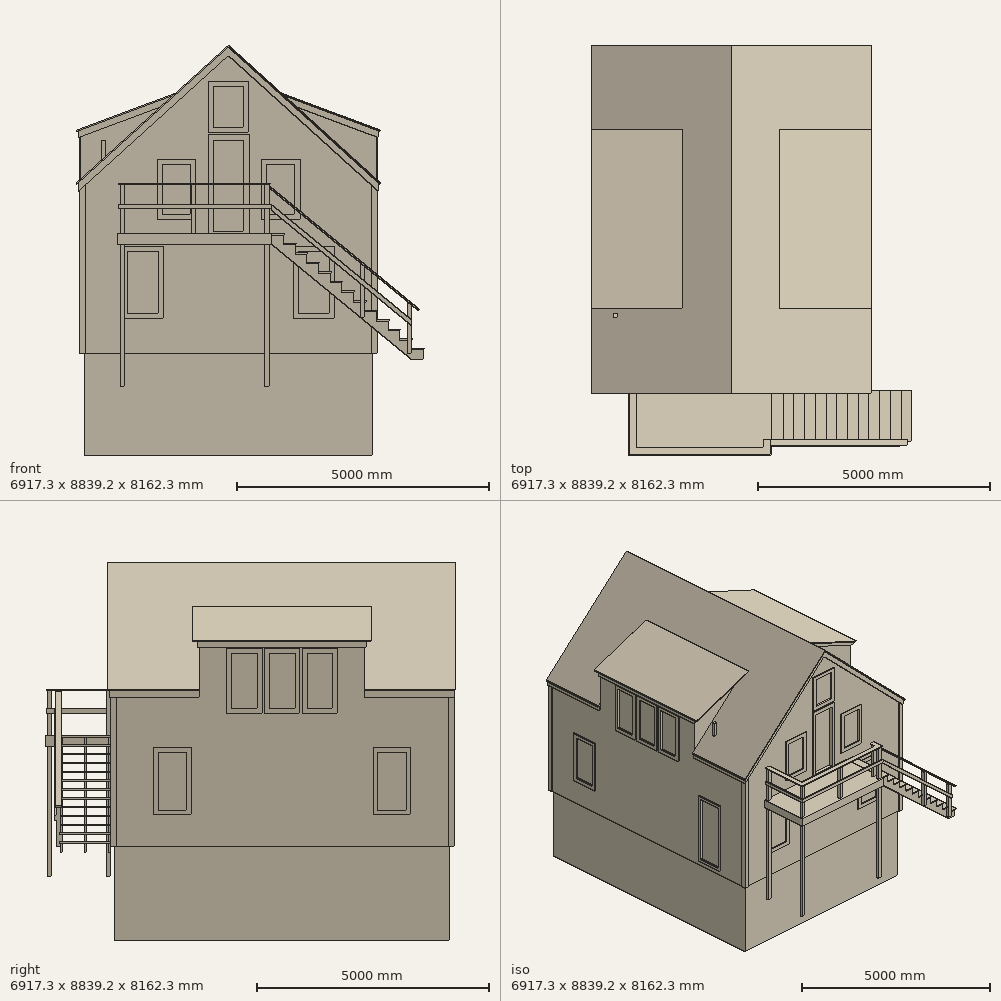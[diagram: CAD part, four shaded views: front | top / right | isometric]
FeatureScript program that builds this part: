
annotation { "Feature Type Name" : "Feature", "Feature Type Description" : "" }
export const myFeature = defineFeature(function(context is Context, id is Id, definition is map)
    precondition{}
    {
        {
            var Q0;
            Q0=qCreatedBy(makeId("Top.planeOp"),FACE);
            var sketch = newSketch(context, id + "F0", { "sketchPlane" : qUnion([Q0])});
            skLineSegment(sketch, "E0.bottom", {"start": v(0, 0) * mm, "end": v(5892.8, 0) * mm});
            skLineSegment(sketch, "E0.top", {"start": v(0, 7366) * mm, "end": v(5892.8, 7366) * mm});
            skLineSegment(sketch, "E0.left", {"start": v(0, 0) * mm, "end": v(0, 7366) * mm});
            skLineSegment(sketch, "E0.right", {"start": v(5892.8, 0) * mm, "end": v(5892.8, 7366) * mm});
            skSolve(sketch);
        }
        {
            var Q0;
            Q0 = qSketchRegion(id + "F0", true);
            extrude(context, id + "F1", {"entities" : qUnion([Q0]), "depth" : 3429 * mm});
        }
        {
            var Q0;
            Q0=makeQuery(id+"F1.opExtrude","SWEPT_FACE",FACE,{"disambiguationData":[OSD([sQuery(id+"F0.wireOp",EDGE,"E0.bottom")])]});
            var sketch = newSketch(context, id + "F2", { "sketchPlane" : qUnion([Q0])});
            skLineSegment(sketch, "E1", {"start": v(0, 3429) * mm, "end": v(2946.4, 6096) * mm});
            skLineSegment(sketch, "E2", {"start": v(2946.4, 6096) * mm, "end": v(5892.8, 3429) * mm});
            skSolve(sketch);
        }
        {
            var Q0;
            Q0=makeQuery(id+"F2.imprint","IMPRINT",FACE,{"disambiguationData":[TD([[makeQuery(id+"F2.imprint","IMPRINT",EDGE,{"derivedFrom":sQuery(id+"F2.wireOp",EDGE,"E1")}),-1.0]])]});
            var Q1;
            Q1=makeQuery(id+"F1.opExtrude","SWEPT_FACE",FACE,{"disambiguationData":[OSD([sQuery(id+"F0.wireOp",EDGE,"E0.top")])]});
            extrude(context, id + "F3", {"entities" : qUnion([Q0]), "operationType" : NewBodyOperationType.ADD, "endBound" : BoundingType.UP_TO_SURFACE, "oppositeDirection" : true, "endBoundEntityFace" : qUnion([Q1]), "depth" : 7315.2 * mm});
        }
        {
            var Q0;
            Q0=makeQuery(id+"F3.opExtrude","SWEPT_EDGE",EDGE,{"disambiguationData":[OSD([sQuery(id+"F2.wireOp",EDGE,"E1"),sQuery(id+"F2.wireOp",EDGE,"E2")])]});
            cPoint(context, id + "F4", {"entities" : qUnion([Q0]), "parameter" : 0.5});
        }
        {
            var Q0;
            {var subQ0=sQuery(id+"F0.wireOp",EDGE,"E0.bottom");Q0=makeQuery(id+"F3.boolean.opBoolean","MERGE",FACE,{"derivedFrom":[makeQuery(id+"F1.opExtrude","SWEPT_FACE",FACE,{"disambiguationData":[OSD([subQ0])]}),makeQuery(id+"F3.opExtrude","CAP_FACE",FACE,{"disambiguationData":[OSD([subQ0,sQuery(id+"F2.wireOp",EDGE,"E1"),sQuery(id+"F2.wireOp",EDGE,"E2")])],"isStart":true})]});}
            var Q1;
            Q1 = qCreatedBy(id + "F4" ,VERTEX);
            cPlane(context, id + "F5", {"entities" : qUnion([Q0, Q1]), "cplaneType" : CPlaneType.PLANE_POINT, "offset" : 25.4 * mm, "width" : 152.4 * mm, "height" : 152.4 * mm});
        }
        {
            var Q0;
            Q0=qCreatedBy(id+"F5.planeOp",FACE);
            var sketch = newSketch(context, id + "F6", { "sketchPlane" : qUnion([Q0])});
            skLineSegment(sketch, "E3", {"start": v(1910.69, 5158.5) * mm, "end": v(0, 4445) * mm});
            skLineSegment(sketch, "E4", {"start": v(0, 4445) * mm, "end": v(0, 3429) * mm});
            skLineSegment(sketch, "E5.MirrorCS", {"start": v(3982.11, 5158.5) * mm, "end": v(5892.8, 4445) * mm});
            skLineSegment(sketch, "E6.MirrorCS", {"start": v(5892.8, 4445) * mm, "end": v(5892.8, 3429) * mm});
            skLineSegment(sketch, "E7", {"start": v(1910.69, 5158.5) * mm, "end": v(0, 3429) * mm});
            skLineSegment(sketch, "E8", {"start": v(3982.11, 5158.5) * mm, "end": v(5892.8, 3429) * mm});
            skSolve(sketch);
        }
        {
            var Q0;
            Q0=makeQuery(id+"F6.imprint","IMPRINT",FACE,{"disambiguationData":[TD([[makeQuery(id+"F6.imprint","IMPRINT",EDGE,{"derivedFrom":sQuery(id+"F6.wireOp",EDGE,"E3")}),1.0]])]});
            var Q1;
            Q1=makeQuery(id+"F6.imprint","IMPRINT",FACE,{"disambiguationData":[TD([[makeQuery(id+"F6.imprint","IMPRINT",EDGE,{"derivedFrom":sQuery(id+"F6.wireOp",EDGE,"E5.MirrorCS")}),-1.0]])]});
            extrude(context, id + "F7", {"entities" : qUnion([Q0, Q1]), "operationType" : NewBodyOperationType.ADD, "endBound" : BoundingType.SYMMETRIC, "depth" : 3556 * mm});
        }
        {
            var Q0;
            Q0=makeQuery(id+"F1.opExtrude","CAP_FACE",FACE,{"disambiguationData":[OSD([sQuery(id+"F0.wireOp",EDGE,"E0.bottom"),sQuery(id+"F0.wireOp",EDGE,"E0.top"),sQuery(id+"F0.wireOp",EDGE,"E0.left"),sQuery(id+"F0.wireOp",EDGE,"E0.right")])],"isStart":true});
            shell(context, id + "F8", {"entities" : qUnion([Q0]), "thickness" : 127 * mm});
        }
        {
            var Q0;
            Q0=qCreatedBy(id+"F5.planeOp",FACE);
            var sketch = newSketch(context, id + "F9", { "sketchPlane" : qUnion([Q0])});
            skLineSegment(sketch, "E9", {"start": v(-38.1, 4430.77) * mm, "end": v(-38.1, 4295.2) * mm});
            skLineSegment(sketch, "E10", {"start": v(-38.1, 4295.2) * mm, "end": v(2946.4, 5409.7) * mm});
            skLineSegment(sketch, "E11", {"start": v(-38.1, 4430.77) * mm, "end": v(2946.4, 5545.26) * mm});
            skLineSegment(sketch, "E12", {"start": v(2946.4, 5409.7) * mm, "end": v(2946.4, 5545.26) * mm});
            skLineSegment(sketch, "E13.MirrorCS", {"start": v(5930.9, 4430.77) * mm, "end": v(2946.4, 5545.26) * mm});
            skLineSegment(sketch, "E14.MirrorCS", {"start": v(5930.9, 4430.77) * mm, "end": v(5930.9, 4295.2) * mm});
            skLineSegment(sketch, "E15.MirrorCS", {"start": v(5930.9, 4295.2) * mm, "end": v(2946.4, 5409.7) * mm});
            skSolve(sketch);
        }
        {
            var Q0;
            Q0=makeQuery(id+"F9.imprint","IMPRINT",FACE,{"disambiguationData":[TD([[makeQuery(id+"F9.imprint","IMPRINT",EDGE,{"derivedFrom":sQuery(id+"F9.wireOp",EDGE,"E12")}),-1.0]])]});
            var Q1;
            Q1=makeQuery(id+"F9.imprint","IMPRINT",FACE,{"disambiguationData":[TD([[makeQuery(id+"F9.imprint","IMPRINT",EDGE,{"derivedFrom":sQuery(id+"F9.wireOp",EDGE,"E9")}),1.0]])]});
            extrude(context, id + "F10", {"entities" : qUnion([Q0, Q1]), "operationType" : NewBodyOperationType.ADD, "endBound" : BoundingType.SYMMETRIC, "depth" : 3642.36 * mm});
        }
        {
            var Q0;
            Q0=qCreatedBy(id+"F5.planeOp",FACE);
            var sketch = newSketch(context, id + "F11", { "sketchPlane" : qUnion([Q0])});
            skLineSegment(sketch, "E16", {"start": v(-76.2, 4443.66) * mm, "end": v(2946.4, 5572.38) * mm});
            skLineSegment(sketch, "E17", {"start": v(-76.2, 4416.54) * mm, "end": v(2946.4, 5545.26) * mm});
            skLineSegment(sketch, "E18", {"start": v(-76.2, 4443.66) * mm, "end": v(-76.2, 4416.54) * mm});
            skLineSegment(sketch, "E19", {"start": v(2946.4, 5572.38) * mm, "end": v(2946.4, 5545.26) * mm});
            skLineSegment(sketch, "E20.MirrorCS", {"start": v(5969, 4443.66) * mm, "end": v(2946.4, 5572.38) * mm});
            skLineSegment(sketch, "E21.MirrorCS", {"start": v(5969, 4416.54) * mm, "end": v(2946.4, 5545.26) * mm});
            skLineSegment(sketch, "E22.MirrorCS", {"start": v(5969, 4443.66) * mm, "end": v(5969, 4416.54) * mm});
            skSolve(sketch);
        }
        {
            var Q0;
            Q0=makeQuery(id+"F11.imprint","IMPRINT",FACE,{"disambiguationData":[TD([[makeQuery(id+"F11.imprint","IMPRINT",EDGE,{"derivedFrom":sQuery(id+"F11.wireOp",EDGE,"E19")}),1.0]])]});
            var Q1;
            Q1=makeQuery(id+"F11.imprint","IMPRINT",FACE,{"disambiguationData":[TD([[makeQuery(id+"F11.imprint","IMPRINT",EDGE,{"derivedFrom":sQuery(id+"F11.wireOp",EDGE,"E16")}),-1.0]])]});
            extrude(context, id + "F12", {"entities" : qUnion([Q0, Q1]), "operationType" : NewBodyOperationType.ADD, "endBound" : BoundingType.SYMMETRIC, "depth" : 3860.8 * mm});
        }
        {
            var Q0;
            {var subQ0=sQuery(id+"F0.wireOp",EDGE,"E0.bottom");Q0=makeQuery(id+"F3.boolean.opBoolean","MERGE",FACE,{"derivedFrom":[makeQuery(id+"F1.opExtrude","SWEPT_FACE",FACE,{"disambiguationData":[OSD([subQ0])]}),makeQuery(id+"F3.opExtrude","CAP_FACE",FACE,{"disambiguationData":[OSD([subQ0,sQuery(id+"F2.wireOp",EDGE,"E1"),sQuery(id+"F2.wireOp",EDGE,"E2")])],"isStart":true})]});}
            var sketch = newSketch(context, id + "F13", { "sketchPlane" : qUnion([Q0])});
            skLineSegment(sketch, "E23", {"start": v(-38.1, 3394.51) * mm, "end": v(2946.4, 6096) * mm});
            skLineSegment(sketch, "E24", {"start": v(-38.1, 3394.51) * mm, "end": v(-38.1, 3223.21) * mm});
            skLineSegment(sketch, "E25", {"start": v(-38.1, 3223.21) * mm, "end": v(2946.4, 5924.7) * mm});
            skLineSegment(sketch, "E26", {"start": v(2946.4, 6096) * mm, "end": v(2946.4, 5924.7) * mm});
            skLineSegment(sketch, "E27.MirrorCS", {"start": v(5930.9, 3394.51) * mm, "end": v(2946.4, 6096) * mm});
            skLineSegment(sketch, "E28.MirrorCS", {"start": v(5930.9, 3223.21) * mm, "end": v(2946.4, 5924.7) * mm});
            skLineSegment(sketch, "E29.MirrorCS", {"start": v(5930.9, 3394.51) * mm, "end": v(5930.9, 3223.21) * mm});
            skSolve(sketch);
        }
        {
            var Q0;
            {var subQ0=sQuery(id+"F13.wireOp",EDGE,"E26");Q0=makeQuery(id+"F13.imprint","IMPRINT",FACE,{"disambiguationData":[TD([[makeQuery(id+"F13.imprint","IMPRINT",EDGE,{"derivedFrom":subQ0}),-1.0]])]});}
            var Q1;
            {var subQ3=sQuery(id+"F13.wireOp",EDGE,"E24");Q1=makeQuery(id+"F13.imprint","IMPRINT",FACE,{"disambiguationData":[TD([[makeQuery(id+"F13.imprint","IMPRINT",EDGE,{"derivedFrom":subQ3}),1.0]])]});}
            var Q2;
            {var subQ3=sQuery(id+"F13.wireOp",EDGE,"E29.MirrorCS");Q2=makeQuery(id+"F13.imprint","IMPRINT",FACE,{"disambiguationData":[TD([[makeQuery(id+"F13.imprint","IMPRINT",EDGE,{"derivedFrom":subQ3}),-1.0]])]});}
            var Q3;
            {var subQ0=sQuery(id+"F13.wireOp",EDGE,"E26");Q3=makeQuery(id+"F13.imprint","IMPRINT",FACE,{"disambiguationData":[TD([[makeQuery(id+"F13.imprint","IMPRINT",EDGE,{"derivedFrom":subQ0}),1.0]])]});}
            extrude(context, id + "F14", {"entities" : qUnion([Q0, Q1, Q2, Q3]), "operationType" : NewBodyOperationType.ADD, "depth" : 38.1 * mm, "hasSecondDirection" : true, "secondDirectionOppositeDirection" : true, "secondDirectionDepth" : 7404.1 * mm});
        }
        {
            var Q0;
            Q0=makeQuery(id+"F14.opExtrude","CAP_FACE",FACE,{"disambiguationData":[OSD([sQuery(id+"F13.wireOp",EDGE,"E23"),sQuery(id+"F13.wireOp",EDGE,"E24"),sQuery(id+"F13.wireOp",EDGE,"E25"),sQuery(id+"F13.wireOp",EDGE,"E27.MirrorCS"),sQuery(id+"F13.wireOp",EDGE,"E28.MirrorCS"),sQuery(id+"F13.wireOp",EDGE,"E29.MirrorCS")])],"isStart":false});
            var sketch = newSketch(context, id + "F15", { "sketchPlane" : qUnion([Q0])});
            skLineSegment(sketch, "E30", {"start": v(-76.2, 3394.29) * mm, "end": v(2946.4, 6130.26) * mm});
            skLineSegment(sketch, "E31", {"start": v(-76.2, 3394.29) * mm, "end": v(-76.2, 3360.03) * mm});
            skLineSegment(sketch, "E32", {"start": v(-76.2, 3360.03) * mm, "end": v(2946.4, 6096) * mm});
            skLineSegment(sketch, "E33", {"start": v(2946.4, 6130.26) * mm, "end": v(2946.4, 6096) * mm});
            skLineSegment(sketch, "E34.MirrorCS", {"start": v(5969, 3394.29) * mm, "end": v(2946.4, 6130.26) * mm});
            skLineSegment(sketch, "E35.MirrorCS", {"start": v(5969, 3360.03) * mm, "end": v(2946.4, 6096) * mm});
            skLineSegment(sketch, "E36.MirrorCS", {"start": v(5969, 3394.29) * mm, "end": v(5969, 3360.03) * mm});
            skSolve(sketch);
        }
        {
            var Q0;
            Q0=makeQuery(id+"F15.imprint","IMPRINT",FACE,{"disambiguationData":[TD([[makeQuery(id+"F15.imprint","IMPRINT",EDGE,{"derivedFrom":sQuery(id+"F15.wireOp",EDGE,"E30")}),-1.0]])]});
            var Q1;
            {var subQ1=sQuery(id+"F15.wireOp",EDGE,"E33");Q1=makeQuery(id+"F15.imprint","IMPRINT",FACE,{"disambiguationData":[TD([[makeQuery(id+"F15.imprint","IMPRINT",EDGE,{"derivedFrom":subQ1}),1.0]])]});}
            extrude(context, id + "F16", {"entities" : qUnion([Q0, Q1]), "operationType" : NewBodyOperationType.ADD, "depth" : 38.1 * mm, "hasSecondDirection" : true, "secondDirectionOppositeDirection" : true, "secondDirectionDepth" : 7454.9 * mm});
        }
        {
            var Q0;
            Q0=makeQuery(id+"F1.opExtrude","CAP_FACE",FACE,{"disambiguationData":[OSD([sQuery(id+"F0.wireOp",EDGE,"E0.bottom"),sQuery(id+"F0.wireOp",EDGE,"E0.top"),sQuery(id+"F0.wireOp",EDGE,"E0.left"),sQuery(id+"F0.wireOp",EDGE,"E0.right")])],"isStart":true});
            var sketch = newSketch(context, id + "F17", { "sketchPlane" : qUnion([Q0])});
            skLineSegment(sketch, "E37.bottom", {"start": v(-25.4, 25.4) * mm, "end": v(101.6, 25.4) * mm});
            skLineSegment(sketch, "E37.top", {"start": v(-25.4, -101.6) * mm, "end": v(101.6, -101.6) * mm});
            skLineSegment(sketch, "E37.left", {"start": v(-25.4, 25.4) * mm, "end": v(-25.4, -101.6) * mm});
            skLineSegment(sketch, "E37.right", {"start": v(101.6, 25.4) * mm, "end": v(101.6, -101.6) * mm});
            skLineSegment(sketch, "E38.bottom", {"start": v(5791.2, 25.4) * mm, "end": v(5918.2, 25.4) * mm});
            skLineSegment(sketch, "E38.top", {"start": v(5791.2, -101.6) * mm, "end": v(5918.2, -101.6) * mm});
            skLineSegment(sketch, "E38.left", {"start": v(5791.2, 25.4) * mm, "end": v(5791.2, -101.6) * mm});
            skLineSegment(sketch, "E38.right", {"start": v(5918.2, 25.4) * mm, "end": v(5918.2, -101.6) * mm});
            skLineSegment(sketch, "E39.MirrorCS", {"start": v(5791.2, -7391.4) * mm, "end": v(5918.2, -7391.4) * mm});
            skLineSegment(sketch, "E40.MirrorCS", {"start": v(-25.4, -7391.4) * mm, "end": v(101.6, -7391.4) * mm});
            skLineSegment(sketch, "E41.MirrorCS", {"start": v(-25.4, -7264.4) * mm, "end": v(101.6, -7264.4) * mm});
            skLineSegment(sketch, "E42.MirrorCS", {"start": v(-25.4, -7391.4) * mm, "end": v(-25.4, -7264.4) * mm});
            skLineSegment(sketch, "E43.MirrorCS", {"start": v(101.6, -7391.4) * mm, "end": v(101.6, -7264.4) * mm});
            skLineSegment(sketch, "E44.MirrorCS", {"start": v(5791.2, -7264.4) * mm, "end": v(5918.2, -7264.4) * mm});
            skLineSegment(sketch, "E45.MirrorCS", {"start": v(5791.2, -7391.4) * mm, "end": v(5791.2, -7264.4) * mm});
            skLineSegment(sketch, "E46.MirrorCS", {"start": v(5918.2, -7391.4) * mm, "end": v(5918.2, -7264.4) * mm});
            skSolve(sketch);
        }
        {
            var Q0;
            Q0 = qSketchRegion(id + "F17", true);
            extrude(context, id + "F18", {"entities" : qUnion([Q0]), "operationType" : NewBodyOperationType.ADD, "oppositeDirection" : true, "depth" : 3352.8 * mm});
        }
        {
            var Q0;
            {var subQ1=sQuery(id+"F0.wireOp",EDGE,"E0.bottom");var subQ2=sQuery(id+"F0.wireOp",EDGE,"E0.left");Q0=makeQuery(id+"F14.boolean.opBoolean","SPLIT",FACE,{"disambiguationData":[TD([makeQuery(id+"F1.opExtrude","SWEPT_FACE",FACE,{"disambiguationData":[OSD([subQ1])]})])],"derivedFrom":makeQuery(id+"F7.boolean.opBoolean","MERGE",FACE,{"derivedFrom":[makeQuery(id+"F1.opExtrude","SWEPT_FACE",FACE,{"disambiguationData":[OSD([subQ2])]}),makeQuery(id+"F7.opExtrude","SWEPT_FACE",FACE,{"disambiguationData":[OSD([sQuery(id+"F6.wireOp",EDGE,"E4")])]})]})});}
            var sketch = newSketch(context, id + "F19", { "sketchPlane" : qUnion([Q0])});
            skLineSegment(sketch, "E47.bottom", {"start": v(-5461, 3938.13) * mm, "end": v(-1905, 3938.13) * mm});
            skLineSegment(sketch, "E47.top", {"start": v(-5461, 1964.71) * mm, "end": v(-1905, 1964.71) * mm});
            skLineSegment(sketch, "E47.left", {"start": v(-5461, 3938.13) * mm, "end": v(-5461, 1964.71) * mm});
            skLineSegment(sketch, "E47.right", {"start": v(-1905, 3938.13) * mm, "end": v(-1905, 1964.71) * mm});
            skSolve(sketch);
        }
        {
            var Q0;
            Q0 = qSketchRegion(id + "F19", true);
            extrude(context, id + "F20", {"entities" : qUnion([Q0]), "operationType" : NewBodyOperationType.REMOVE, "depth" : 1270 * mm});
        }
        {
            var Q0;
            {var subQ1=sQuery(id+"F0.wireOp",EDGE,"E0.bottom");var subQ2=sQuery(id+"F0.wireOp",EDGE,"E0.right");Q0=makeQuery(id+"F14.boolean.opBoolean","SPLIT",FACE,{"disambiguationData":[TD([makeQuery(id+"F1.opExtrude","SWEPT_FACE",FACE,{"disambiguationData":[OSD([subQ1])]})])],"derivedFrom":makeQuery(id+"F7.boolean.opBoolean","MERGE",FACE,{"derivedFrom":[makeQuery(id+"F1.opExtrude","SWEPT_FACE",FACE,{"disambiguationData":[OSD([subQ2])]}),makeQuery(id+"F7.opExtrude","SWEPT_FACE",FACE,{"disambiguationData":[OSD([sQuery(id+"F6.wireOp",EDGE,"E6.MirrorCS")])]})]})});}
            var sketch = newSketch(context, id + "F21", { "sketchPlane" : qUnion([Q0])});
            skLineSegment(sketch, "E48.bottom", {"start": v(1905, 3765.85) * mm, "end": v(5461, 3765.85) * mm});
            skLineSegment(sketch, "E48.top", {"start": v(1905, 1949.05) * mm, "end": v(5461, 1949.05) * mm});
            skLineSegment(sketch, "E48.left", {"start": v(1905, 3765.85) * mm, "end": v(1905, 1949.05) * mm});
            skLineSegment(sketch, "E48.right", {"start": v(5461, 3765.85) * mm, "end": v(5461, 1949.05) * mm});
            skSolve(sketch);
        }
        {
            var Q0;
            Q0 = qSketchRegion(id + "F21", true);
            extrude(context, id + "F22", {"entities" : qUnion([Q0]), "operationType" : NewBodyOperationType.REMOVE, "depth" : 1092.2 * mm});
        }
        {
            var Q0;
            {var subQ0=sQuery(id+"F0.wireOp",EDGE,"E0.bottom");Q0=makeQuery(id+"F3.boolean.opBoolean","MERGE",FACE,{"derivedFrom":[makeQuery(id+"F1.opExtrude","SWEPT_FACE",FACE,{"disambiguationData":[OSD([subQ0])]}),makeQuery(id+"F3.opExtrude","CAP_FACE",FACE,{"disambiguationData":[OSD([subQ0,sQuery(id+"F2.wireOp",EDGE,"E1"),sQuery(id+"F2.wireOp",EDGE,"E2")])],"isStart":true})]});}
            var sketch = newSketch(context, id + "F23", { "sketchPlane" : qUnion([Q0])});
            skLineSegment(sketch, "E49.bottom", {"start": v(2552.7, 5416.7) * mm, "end": v(3340.1, 5416.7) * mm});
            skLineSegment(sketch, "E49.top", {"start": v(2552.7, 4400.7) * mm, "end": v(3340.1, 4400.7) * mm});
            skLineSegment(sketch, "E49.left", {"start": v(2552.7, 5416.7) * mm, "end": v(2552.7, 4400.7) * mm});
            skLineSegment(sketch, "E49.right", {"start": v(3340.1, 5416.7) * mm, "end": v(3340.1, 4400.7) * mm});
            skLineSegment(sketch, "E50.bottom", {"start": v(2540, 4349.9) * mm, "end": v(3352.8, 4349.9) * mm});
            skLineSegment(sketch, "E50.top", {"start": v(2540, 2317.9) * mm, "end": v(3352.8, 2317.9) * mm});
            skLineSegment(sketch, "E50.left", {"start": v(2540, 4349.9) * mm, "end": v(2540, 2317.9) * mm});
            skLineSegment(sketch, "E50.right", {"start": v(3352.8, 4349.9) * mm, "end": v(3352.8, 2317.9) * mm});
            skLineSegment(sketch, "E51.bottom", {"start": v(1524, 3867.3) * mm, "end": v(2286, 3867.3) * mm});
            skLineSegment(sketch, "E51.top", {"start": v(1524, 2673.5) * mm, "end": v(2286, 2673.5) * mm});
            skLineSegment(sketch, "E51.left", {"start": v(1524, 3867.3) * mm, "end": v(1524, 2673.5) * mm});
            skLineSegment(sketch, "E51.right", {"start": v(2286, 3867.3) * mm, "end": v(2286, 2673.5) * mm});
            skLineSegment(sketch, "E52.bottom", {"start": v(838.2, 2133.6) * mm, "end": v(1651, 2133.6) * mm});
            skLineSegment(sketch, "E52.top", {"start": v(838.2, 685.8) * mm, "end": v(1651, 685.8) * mm});
            skLineSegment(sketch, "E52.left", {"start": v(838.2, 2133.6) * mm, "end": v(838.2, 685.8) * mm});
            skLineSegment(sketch, "E52.right", {"start": v(1651, 2133.6) * mm, "end": v(1651, 685.8) * mm});
            skLineSegment(sketch, "E53", {"start": v(2946.4, 5416.7) * mm, "end": v(2946.4, 5924.7) * mm});
            skLineSegment(sketch, "E54.MirrorCS", {"start": v(5124.83, 5416.7) * mm, "end": v(5124.83, 5924.7) * mm});
            skLineSegment(sketch, "E55.MirrorCS", {"start": v(4241.8, 2133.6) * mm, "end": v(4241.8, 685.8) * mm});
            skLineSegment(sketch, "E56.MirrorCS", {"start": v(5054.6, 2133.6) * mm, "end": v(5054.6, 685.8) * mm});
            skLineSegment(sketch, "E57.MirrorCS", {"start": v(4368.8, 3867.3) * mm, "end": v(3606.8, 3867.3) * mm});
            skLineSegment(sketch, "E58.MirrorCS", {"start": v(5054.6, 685.8) * mm, "end": v(4241.8, 685.8) * mm});
            skLineSegment(sketch, "E59.MirrorCS", {"start": v(4368.8, 2673.5) * mm, "end": v(3606.8, 2673.5) * mm});
            skLineSegment(sketch, "E60.MirrorCS", {"start": v(4368.8, 3867.3) * mm, "end": v(4368.8, 2673.5) * mm});
            skLineSegment(sketch, "E61.MirrorCS", {"start": v(3606.8, 3867.3) * mm, "end": v(3606.8, 2673.5) * mm});
            skLineSegment(sketch, "E62.MirrorCS", {"start": v(5054.6, 2133.6) * mm, "end": v(4241.8, 2133.6) * mm});
            skSolve(sketch);
        }
        {
            var Q0;
            Q0=makeQuery(id+"F23.imprint","IMPRINT",FACE,{"disambiguationData":[TD([[makeQuery(id+"F23.imprint","IMPRINT",EDGE,{"derivedFrom":sQuery(id+"F23.wireOp",EDGE,"E51.bottom")}),-1.0]])]});
            var Q1;
            Q1=makeQuery(id+"F23.imprint","IMPRINT",FACE,{"disambiguationData":[TD([[makeQuery(id+"F23.imprint","IMPRINT",EDGE,{"derivedFrom":sQuery(id+"F23.wireOp",EDGE,"E49.top")}),1.0]])]});
            var Q2;
            Q2=makeQuery(id+"F23.imprint","IMPRINT",FACE,{"disambiguationData":[TD([[makeQuery(id+"F23.imprint","IMPRINT",EDGE,{"derivedFrom":sQuery(id+"F23.wireOp",EDGE,"E50.bottom")}),-1.0]])]});
            var Q3;
            Q3=makeQuery(id+"F23.imprint","IMPRINT",FACE,{"disambiguationData":[TD([[makeQuery(id+"F23.imprint","IMPRINT",EDGE,{"derivedFrom":sQuery(id+"F23.wireOp",EDGE,"E57.MirrorCS")}),1.0]])]});
            var Q4;
            Q4=makeQuery(id+"F23.imprint","IMPRINT",FACE,{"disambiguationData":[TD([[makeQuery(id+"F23.imprint","IMPRINT",EDGE,{"derivedFrom":sQuery(id+"F23.wireOp",EDGE,"E55.MirrorCS")}),1.0]])]});
            var Q5;
            Q5=makeQuery(id+"F23.imprint","IMPRINT",FACE,{"disambiguationData":[TD([[makeQuery(id+"F23.imprint","IMPRINT",EDGE,{"derivedFrom":sQuery(id+"F23.wireOp",EDGE,"E52.bottom")}),-1.0]])]});
            extrude(context, id + "F24", {"entities" : qUnion([Q0, Q1, Q2, Q3, Q4, Q5]), "operationType" : NewBodyOperationType.ADD, "depth" : 25.4 * mm});
        }
        {
            var Q0;
            Q0=makeQuery(id+"F24.opExtrude","CAP_FACE",FACE,{"disambiguationData":[OSD([sQuery(id+"F23.wireOp",EDGE,"E52.bottom"),sQuery(id+"F23.wireOp",EDGE,"E52.top"),sQuery(id+"F23.wireOp",EDGE,"E52.left"),sQuery(id+"F23.wireOp",EDGE,"E52.right")])],"isStart":false});
            var sketch = newSketch(context, id + "F25", { "sketchPlane" : qUnion([Q0])});
            skLineSegment(sketch, "E63.0", {"start": v(1549.4, 2032) * mm, "end": v(939.8, 2032) * mm});
            skLineSegment(sketch, "E63.1", {"start": v(1549.4, 787.4) * mm, "end": v(1549.4, 2032) * mm});
            skLineSegment(sketch, "E63.2", {"start": v(939.8, 787.4) * mm, "end": v(1549.4, 787.4) * mm});
            skLineSegment(sketch, "E63.3", {"start": v(939.8, 2032) * mm, "end": v(939.8, 787.4) * mm});
            skLineSegment(sketch, "E64.0", {"start": v(4953, 2032) * mm, "end": v(4343.4, 2032) * mm});
            skLineSegment(sketch, "E64.1", {"start": v(4953, 787.4) * mm, "end": v(4953, 2032) * mm});
            skLineSegment(sketch, "E64.2", {"start": v(4343.4, 787.4) * mm, "end": v(4953, 787.4) * mm});
            skLineSegment(sketch, "E64.3", {"start": v(4343.4, 2032) * mm, "end": v(4343.4, 787.4) * mm});
            skLineSegment(sketch, "E65.0", {"start": v(2184.4, 3765.7) * mm, "end": v(1625.6, 3765.7) * mm});
            skLineSegment(sketch, "E65.1", {"start": v(2184.4, 2775.1) * mm, "end": v(2184.4, 3765.7) * mm});
            skLineSegment(sketch, "E65.2", {"start": v(1625.6, 2775.1) * mm, "end": v(2184.4, 2775.1) * mm});
            skLineSegment(sketch, "E65.3", {"start": v(1625.6, 3765.7) * mm, "end": v(1625.6, 2775.1) * mm});
            skLineSegment(sketch, "E66.0", {"start": v(4267.2, 2775.1) * mm, "end": v(4267.2, 3765.7) * mm});
            skLineSegment(sketch, "E66.1", {"start": v(3708.4, 2775.1) * mm, "end": v(4267.2, 2775.1) * mm});
            skLineSegment(sketch, "E66.2", {"start": v(3708.4, 3765.7) * mm, "end": v(3708.4, 2775.1) * mm});
            skLineSegment(sketch, "E66.3", {"start": v(4267.2, 3765.7) * mm, "end": v(3708.4, 3765.7) * mm});
            skLineSegment(sketch, "E67.0", {"start": v(3238.5, 5315.1) * mm, "end": v(2654.3, 5315.1) * mm});
            skLineSegment(sketch, "E67.1", {"start": v(3238.5, 4502.3) * mm, "end": v(3238.5, 5315.1) * mm});
            skLineSegment(sketch, "E67.2", {"start": v(2654.3, 4502.3) * mm, "end": v(3238.5, 4502.3) * mm});
            skLineSegment(sketch, "E67.3", {"start": v(2654.3, 5315.1) * mm, "end": v(2654.3, 4502.3) * mm});
            skLineSegment(sketch, "E68.0", {"start": v(3251.2, 4248.3) * mm, "end": v(2641.6, 4248.3) * mm});
            skLineSegment(sketch, "E68.1", {"start": v(3251.2, 2419.5) * mm, "end": v(3251.2, 4248.3) * mm});
            skLineSegment(sketch, "E68.2", {"start": v(2641.6, 2419.5) * mm, "end": v(3251.2, 2419.5) * mm});
            skLineSegment(sketch, "E68.3", {"start": v(2641.6, 4248.3) * mm, "end": v(2641.6, 2419.5) * mm});
            skSolve(sketch);
        }
        {
            var Q0;
            Q0=makeQuery(id+"F25.imprint","IMPRINT",FACE,{"disambiguationData":[TD([[makeQuery(id+"F25.imprint","IMPRINT",EDGE,{"derivedFrom":sQuery(id+"F25.wireOp",EDGE,"E63.0")}),1.0]])]});
            var Q1;
            Q1=makeQuery(id+"F25.imprint","IMPRINT",FACE,{"disambiguationData":[TD([[makeQuery(id+"F25.imprint","IMPRINT",EDGE,{"derivedFrom":sQuery(id+"F25.wireOp",EDGE,"E65.0")}),1.0]])]});
            var Q2;
            Q2=makeQuery(id+"F25.imprint","IMPRINT",FACE,{"disambiguationData":[TD([[makeQuery(id+"F25.imprint","IMPRINT",EDGE,{"derivedFrom":sQuery(id+"F25.wireOp",EDGE,"E67.0")}),1.0]])]});
            var Q3;
            Q3=makeQuery(id+"F25.imprint","IMPRINT",FACE,{"disambiguationData":[TD([[makeQuery(id+"F25.imprint","IMPRINT",EDGE,{"derivedFrom":sQuery(id+"F25.wireOp",EDGE,"E66.0")}),1.0]])]});
            var Q4;
            Q4=makeQuery(id+"F25.imprint","IMPRINT",FACE,{"disambiguationData":[TD([[makeQuery(id+"F25.imprint","IMPRINT",EDGE,{"derivedFrom":sQuery(id+"F25.wireOp",EDGE,"E64.0")}),1.0]])]});
            extrude(context, id + "F26", {"entities" : qUnion([Q0, Q1, Q2, Q3, Q4]), "operationType" : NewBodyOperationType.REMOVE, "oppositeDirection" : true, "depth" : 50.8 * mm});
        }
        {
            var Q0;
            Q0=makeQuery(id+"F24.opExtrude","CAP_FACE",FACE,{"disambiguationData":[OSD([sQuery(id+"F23.wireOp",EDGE,"E50.bottom"),sQuery(id+"F23.wireOp",EDGE,"E50.top"),sQuery(id+"F23.wireOp",EDGE,"E50.left"),sQuery(id+"F23.wireOp",EDGE,"E50.right")])],"isStart":false});
            var sketch = newSketch(context, id + "F27", { "sketchPlane" : qUnion([Q0])});
            skLineSegment(sketch, "E69.0", {"start": v(3251.2, 4248.3) * mm, "end": v(2641.6, 4248.3) * mm});
            skLineSegment(sketch, "E69.1", {"start": v(3251.2, 2419.5) * mm, "end": v(3251.2, 4248.3) * mm});
            skLineSegment(sketch, "E69.2", {"start": v(2641.6, 2419.5) * mm, "end": v(3251.2, 2419.5) * mm});
            skLineSegment(sketch, "E69.3", {"start": v(2641.6, 4248.3) * mm, "end": v(2641.6, 2419.5) * mm});
            skSolve(sketch);
        }
        {
            var Q0;
            Q0 = qSketchRegion(id + "F27", true);
            extrude(context, id + "F28", {"entities" : qUnion([Q0]), "operationType" : NewBodyOperationType.REMOVE, "oppositeDirection" : true, "depth" : 101.6 * mm});
        }
        {
            var Q0;
            {var subQ1=sQuery(id+"F2.wireOp",EDGE,"E2");var subQ2=sQuery(id+"F0.wireOp",EDGE,"E0.bottom");var subQ3=sQuery(id+"F0.wireOp",EDGE,"E0.right");var subQ4=sQuery(id+"F6.wireOp",EDGE,"E6.MirrorCS");var subQ5=makeQuery(id+"F7.boolean.opBoolean","MERGE",FACE,{"derivedFrom":[makeQuery(id+"F1.opExtrude","SWEPT_FACE",FACE,{"disambiguationData":[OSD([subQ3])]}),makeQuery(id+"F7.opExtrude","SWEPT_FACE",FACE,{"disambiguationData":[OSD([subQ4])]})]});Q0=makeQuery(id+"F22.boolean.opBoolean","MERGE",FACE,{"derivedFrom":[makeQuery(id+"F14.boolean.opBoolean","SPLIT",FACE,{"disambiguationData":[TD([makeQuery(id+"F3.opExtrude","SWEPT_FACE",FACE,{"disambiguationData":[OSD([subQ1])]})])],"derivedFrom":subQ5}),makeQuery(id+"F14.boolean.opBoolean","SPLIT",FACE,{"disambiguationData":[TD([makeQuery(id+"F1.opExtrude","SWEPT_FACE",FACE,{"disambiguationData":[OSD([subQ2])]})])],"derivedFrom":subQ5}),makeQuery(id+"F22.opExtrude","CAP_FACE",FACE,{"disambiguationData":[OSD([sQuery(id+"F21.wireOp",EDGE,"E48.bottom"),sQuery(id+"F21.wireOp",EDGE,"E48.top"),sQuery(id+"F21.wireOp",EDGE,"E48.left"),sQuery(id+"F21.wireOp",EDGE,"E48.right")])],"isStart":true})]});}
            var sketch = newSketch(context, id + "F29", { "sketchPlane" : qUnion([Q0])});
            skLineSegment(sketch, "E70.bottom", {"start": v(3302, 4269.8) * mm, "end": v(4064, 4269.8) * mm});
            skLineSegment(sketch, "E70.top", {"start": v(3302, 2872.8) * mm, "end": v(4064, 2872.8) * mm});
            skLineSegment(sketch, "E70.left", {"start": v(3302, 4269.8) * mm, "end": v(3302, 2872.8) * mm});
            skLineSegment(sketch, "E70.right", {"start": v(4064, 4269.8) * mm, "end": v(4064, 2872.8) * mm});
            skLineSegment(sketch, "E71.bottom", {"start": v(2489.2, 4269.8) * mm, "end": v(3251.2, 4269.8) * mm});
            skLineSegment(sketch, "E71.top", {"start": v(2489.2, 2872.8) * mm, "end": v(3251.2, 2872.8) * mm});
            skLineSegment(sketch, "E71.left", {"start": v(2489.2, 4269.8) * mm, "end": v(2489.2, 2872.8) * mm});
            skLineSegment(sketch, "E71.right", {"start": v(3251.2, 4269.8) * mm, "end": v(3251.2, 2872.8) * mm});
            skLineSegment(sketch, "E72.bottom", {"start": v(4114.8, 4269.8) * mm, "end": v(4876.8, 4269.8) * mm});
            skLineSegment(sketch, "E72.top", {"start": v(4114.8, 2872.8) * mm, "end": v(4876.8, 2872.8) * mm});
            skLineSegment(sketch, "E72.left", {"start": v(4114.8, 4269.8) * mm, "end": v(4114.8, 2872.8) * mm});
            skLineSegment(sketch, "E72.right", {"start": v(4876.8, 4269.8) * mm, "end": v(4876.8, 2872.8) * mm});
            skLineSegment(sketch, "E73.bottom", {"start": v(5638.8, 2133.6) * mm, "end": v(6451.6, 2133.6) * mm});
            skLineSegment(sketch, "E73.top", {"start": v(5638.8, 685.8) * mm, "end": v(6451.6, 685.8) * mm});
            skLineSegment(sketch, "E73.left", {"start": v(5638.8, 2133.6) * mm, "end": v(5638.8, 685.8) * mm});
            skLineSegment(sketch, "E73.right", {"start": v(6451.6, 2133.6) * mm, "end": v(6451.6, 685.8) * mm});
            skLineSegment(sketch, "E74.MirrorCS", {"start": v(1727.2, 685.8) * mm, "end": v(914.4, 685.8) * mm});
            skLineSegment(sketch, "E75.MirrorCS", {"start": v(914.4, 2133.6) * mm, "end": v(914.4, 685.8) * mm});
            skLineSegment(sketch, "E76.MirrorCS", {"start": v(1727.2, 2133.6) * mm, "end": v(1727.2, 685.8) * mm});
            skLineSegment(sketch, "E77.MirrorCS", {"start": v(1727.2, 2133.6) * mm, "end": v(914.4, 2133.6) * mm});
            skSolve(sketch);
        }
        {
            var Q0;
            Q0 = qSketchRegion(id + "F29", true);
            extrude(context, id + "F30", {"entities" : qUnion([Q0]), "operationType" : NewBodyOperationType.ADD, "depth" : 25.4 * mm});
        }
        {
            var Q0;
            {var subQ1=sQuery(id+"F2.wireOp",EDGE,"E1");var subQ2=sQuery(id+"F0.wireOp",EDGE,"E0.bottom");var subQ3=sQuery(id+"F0.wireOp",EDGE,"E0.left");var subQ4=sQuery(id+"F6.wireOp",EDGE,"E4");var subQ5=makeQuery(id+"F7.boolean.opBoolean","MERGE",FACE,{"derivedFrom":[makeQuery(id+"F1.opExtrude","SWEPT_FACE",FACE,{"disambiguationData":[OSD([subQ3])]}),makeQuery(id+"F7.opExtrude","SWEPT_FACE",FACE,{"disambiguationData":[OSD([subQ4])]})]});Q0=makeQuery(id+"F20.boolean.opBoolean","MERGE",FACE,{"derivedFrom":[makeQuery(id+"F14.boolean.opBoolean","SPLIT",FACE,{"disambiguationData":[TD([makeQuery(id+"F3.opExtrude","SWEPT_FACE",FACE,{"disambiguationData":[OSD([subQ1])]})])],"derivedFrom":subQ5}),makeQuery(id+"F14.boolean.opBoolean","SPLIT",FACE,{"disambiguationData":[TD([makeQuery(id+"F1.opExtrude","SWEPT_FACE",FACE,{"disambiguationData":[OSD([subQ2])]})])],"derivedFrom":subQ5}),makeQuery(id+"F20.opExtrude","CAP_FACE",FACE,{"disambiguationData":[OSD([sQuery(id+"F19.wireOp",EDGE,"E47.bottom"),sQuery(id+"F19.wireOp",EDGE,"E47.top"),sQuery(id+"F19.wireOp",EDGE,"E47.left"),sQuery(id+"F19.wireOp",EDGE,"E47.right")])],"isStart":true})]});}
            var sketch = newSketch(context, id + "F31", { "sketchPlane" : qUnion([Q0])});
            skLineSegment(sketch, "E78.0.2", {"start": v(-1727.2, 2133.6) * mm, "end": v(-914.4, 2133.6) * mm});
            skLineSegment(sketch, "E79.0.0", {"start": v(-3251.2, 4269.8) * mm, "end": v(-2489.2, 4269.8) * mm});
            skLineSegment(sketch, "E79.0.1", {"start": v(-2489.2, 4269.8) * mm, "end": v(-2489.2, 2872.8) * mm});
            skLineSegment(sketch, "E79.0.2", {"start": v(-2489.2, 2872.8) * mm, "end": v(-3251.2, 2872.8) * mm});
            skLineSegment(sketch, "E79.0.3", {"start": v(-3251.2, 2872.8) * mm, "end": v(-3251.2, 4269.8) * mm});
            skLineSegment(sketch, "E80.0.0", {"start": v(-4064, 4269.8) * mm, "end": v(-3302, 4269.8) * mm});
            skLineSegment(sketch, "E80.0.1", {"start": v(-3302, 4269.8) * mm, "end": v(-3302, 2872.8) * mm});
            skLineSegment(sketch, "E80.0.2", {"start": v(-3302, 2872.8) * mm, "end": v(-4064, 2872.8) * mm});
            skLineSegment(sketch, "E80.0.3", {"start": v(-4064, 2872.8) * mm, "end": v(-4064, 4269.8) * mm});
            skLineSegment(sketch, "E81.0.0", {"start": v(-4876.8, 4269.8) * mm, "end": v(-4114.8, 4269.8) * mm});
            skLineSegment(sketch, "E81.0.1", {"start": v(-4114.8, 4269.8) * mm, "end": v(-4114.8, 2872.8) * mm});
            skLineSegment(sketch, "E81.0.2", {"start": v(-4114.8, 2872.8) * mm, "end": v(-4876.8, 2872.8) * mm});
            skLineSegment(sketch, "E81.0.3", {"start": v(-4876.8, 2872.8) * mm, "end": v(-4876.8, 4269.8) * mm});
            skLineSegment(sketch, "E82.0.0", {"start": v(-6451.6, 2133.6) * mm, "end": v(-5638.8, 2133.6) * mm});
            skLineSegment(sketch, "E82.0.1", {"start": v(-5638.8, 2133.6) * mm, "end": v(-5638.8, 685.8) * mm});
            skLineSegment(sketch, "E82.0.2", {"start": v(-5638.8, 685.8) * mm, "end": v(-6451.6, 685.8) * mm});
            skLineSegment(sketch, "E82.0.3", {"start": v(-6451.6, 685.8) * mm, "end": v(-6451.6, 2133.6) * mm});
            skLineSegment(sketch, "E83", {"start": v(-1727.2, 2133.6) * mm, "end": v(-1727.2, 127) * mm});
            skLineSegment(sketch, "E84", {"start": v(-1727.2, 127) * mm, "end": v(-914.4, 127) * mm});
            skLineSegment(sketch, "E85", {"start": v(-914.4, 127) * mm, "end": v(-914.4, 2133.6) * mm});
            skSolve(sketch);
        }
        {
            var Q0;
            Q0 = qSketchRegion(id + "F31", true);
            extrude(context, id + "F32", {"entities" : qUnion([Q0]), "operationType" : NewBodyOperationType.ADD, "depth" : 25.4 * mm});
        }
        {
            var Q0;
            Q0=makeQuery(id+"F30.opExtrude","CAP_FACE",FACE,{"disambiguationData":[OSD([sQuery(id+"F29.wireOp",EDGE,"E74.MirrorCS"),sQuery(id+"F29.wireOp",EDGE,"E75.MirrorCS"),sQuery(id+"F29.wireOp",EDGE,"E76.MirrorCS"),sQuery(id+"F29.wireOp",EDGE,"E77.MirrorCS")])],"isStart":false});
            var sketch = newSketch(context, id + "F33", { "sketchPlane" : qUnion([Q0])});
            skLineSegment(sketch, "E86.0", {"start": v(3149.6, 4168.2) * mm, "end": v(2590.8, 4168.2) * mm});
            skLineSegment(sketch, "E86.1", {"start": v(3149.6, 2974.4) * mm, "end": v(3149.6, 4168.2) * mm});
            skLineSegment(sketch, "E86.2", {"start": v(2590.8, 2974.4) * mm, "end": v(3149.6, 2974.4) * mm});
            skLineSegment(sketch, "E86.3", {"start": v(2590.8, 4168.2) * mm, "end": v(2590.8, 2974.4) * mm});
            skLineSegment(sketch, "E87.0", {"start": v(3962.4, 4168.2) * mm, "end": v(3403.6, 4168.2) * mm});
            skLineSegment(sketch, "E87.1", {"start": v(3962.4, 2974.4) * mm, "end": v(3962.4, 4168.2) * mm});
            skLineSegment(sketch, "E87.2", {"start": v(3403.6, 2974.4) * mm, "end": v(3962.4, 2974.4) * mm});
            skLineSegment(sketch, "E87.3", {"start": v(3403.6, 4168.2) * mm, "end": v(3403.6, 2974.4) * mm});
            skLineSegment(sketch, "E88.0", {"start": v(4775.2, 4168.2) * mm, "end": v(4216.4, 4168.2) * mm});
            skLineSegment(sketch, "E88.1", {"start": v(4775.2, 2974.4) * mm, "end": v(4775.2, 4168.2) * mm});
            skLineSegment(sketch, "E88.2", {"start": v(4216.4, 2974.4) * mm, "end": v(4775.2, 2974.4) * mm});
            skLineSegment(sketch, "E88.3", {"start": v(4216.4, 4168.2) * mm, "end": v(4216.4, 2974.4) * mm});
            skLineSegment(sketch, "E89.0", {"start": v(6350, 2032) * mm, "end": v(5740.4, 2032) * mm});
            skLineSegment(sketch, "E89.1", {"start": v(6350, 787.4) * mm, "end": v(6350, 2032) * mm});
            skLineSegment(sketch, "E89.2", {"start": v(5740.4, 787.4) * mm, "end": v(6350, 787.4) * mm});
            skLineSegment(sketch, "E89.3", {"start": v(5740.4, 2032) * mm, "end": v(5740.4, 787.4) * mm});
            skLineSegment(sketch, "E90.0", {"start": v(1016, 787.4) * mm, "end": v(1625.6, 787.4) * mm});
            skLineSegment(sketch, "E90.1", {"start": v(1016, 2032) * mm, "end": v(1016, 787.4) * mm});
            skLineSegment(sketch, "E90.2", {"start": v(1625.6, 2032) * mm, "end": v(1016, 2032) * mm});
            skLineSegment(sketch, "E90.3", {"start": v(1625.6, 787.4) * mm, "end": v(1625.6, 2032) * mm});
            skSolve(sketch);
        }
        {
            var Q0;
            Q0 = qSketchRegion(id + "F33", true);
            extrude(context, id + "F34", {"entities" : qUnion([Q0]), "operationType" : NewBodyOperationType.REMOVE, "oppositeDirection" : true, "depth" : 50.8 * mm});
        }
        {
            var Q0;
            Q0=makeQuery(id+"F32.opExtrude","CAP_FACE",FACE,{"disambiguationData":[OSD([sQuery(id+"F31.wireOp",EDGE,"E82.0.0"),sQuery(id+"F31.wireOp",EDGE,"E82.0.1"),sQuery(id+"F31.wireOp",EDGE,"E82.0.2"),sQuery(id+"F31.wireOp",EDGE,"E82.0.3")])],"isStart":false});
            var sketch = newSketch(context, id + "F35", { "sketchPlane" : qUnion([Q0])});
            skLineSegment(sketch, "E91.0", {"start": v(-5740.4, 2032) * mm, "end": v(-6350, 2032) * mm});
            skLineSegment(sketch, "E91.1", {"start": v(-5740.4, 787.4) * mm, "end": v(-5740.4, 2032) * mm});
            skLineSegment(sketch, "E91.2", {"start": v(-6350, 787.4) * mm, "end": v(-5740.4, 787.4) * mm});
            skLineSegment(sketch, "E91.3", {"start": v(-6350, 2032) * mm, "end": v(-6350, 787.4) * mm});
            skLineSegment(sketch, "E92.0", {"start": v(-4216.4, 4168.2) * mm, "end": v(-4775.2, 4168.2) * mm});
            skLineSegment(sketch, "E92.1", {"start": v(-4216.4, 2974.4) * mm, "end": v(-4216.4, 4168.2) * mm});
            skLineSegment(sketch, "E92.2", {"start": v(-4775.2, 2974.4) * mm, "end": v(-4216.4, 2974.4) * mm});
            skLineSegment(sketch, "E92.3", {"start": v(-4775.2, 4168.2) * mm, "end": v(-4775.2, 2974.4) * mm});
            skLineSegment(sketch, "E93.0", {"start": v(-3403.6, 4168.2) * mm, "end": v(-3962.4, 4168.2) * mm});
            skLineSegment(sketch, "E93.1", {"start": v(-3403.6, 2974.4) * mm, "end": v(-3403.6, 4168.2) * mm});
            skLineSegment(sketch, "E93.2", {"start": v(-3962.4, 2974.4) * mm, "end": v(-3403.6, 2974.4) * mm});
            skLineSegment(sketch, "E93.3", {"start": v(-3962.4, 4168.2) * mm, "end": v(-3962.4, 2974.4) * mm});
            skLineSegment(sketch, "E94.0", {"start": v(-2590.8, 4168.2) * mm, "end": v(-3149.6, 4168.2) * mm});
            skLineSegment(sketch, "E94.1", {"start": v(-2590.8, 2974.4) * mm, "end": v(-2590.8, 4168.2) * mm});
            skLineSegment(sketch, "E94.2", {"start": v(-3149.6, 2974.4) * mm, "end": v(-2590.8, 2974.4) * mm});
            skLineSegment(sketch, "E94.3", {"start": v(-3149.6, 4168.2) * mm, "end": v(-3149.6, 2974.4) * mm});
            skLineSegment(sketch, "E95.0", {"start": v(-990.6, 2057.4) * mm, "end": v(-1651, 2057.4) * mm});
            skLineSegment(sketch, "E95.1", {"start": v(-990.6, 203.2) * mm, "end": v(-990.6, 2057.4) * mm});
            skLineSegment(sketch, "E95.2", {"start": v(-1651, 203.2) * mm, "end": v(-990.6, 203.2) * mm});
            skLineSegment(sketch, "E95.3", {"start": v(-1651, 2057.4) * mm, "end": v(-1651, 203.2) * mm});
            skSolve(sketch);
        }
        {
            var Q0;
            Q0 = qSketchRegion(id + "F35", true);
            extrude(context, id + "F36", {"entities" : qUnion([Q0]), "operationType" : NewBodyOperationType.REMOVE, "oppositeDirection" : true, "depth" : 50.8 * mm});
        }
        {
            var Q0;
            {var subQ0=sQuery(id+"F0.wireOp",EDGE,"E0.top");Q0=makeQuery(id+"F3.boolean.opBoolean","MERGE",FACE,{"derivedFrom":[makeQuery(id+"F1.opExtrude","SWEPT_FACE",FACE,{"disambiguationData":[OSD([subQ0])]}),makeQuery(id+"F3.opExtrude","CAP_FACE",FACE,{"disambiguationData":[OSD([subQ0])],"isStart":false})]});}
            var sketch = newSketch(context, id + "F37", { "sketchPlane" : qUnion([Q0])});
            skLineSegment(sketch, "E96", {"start": v(-2946.4, 5924.7) * mm, "end": v(-2946.4, 3750.59) * mm});
            skLineSegment(sketch, "E97.bottom", {"start": v(-4318, 3987.8) * mm, "end": v(-3606.8, 3987.8) * mm});
            skLineSegment(sketch, "E97.top", {"start": v(-4318, 2794) * mm, "end": v(-3606.8, 2794) * mm});
            skLineSegment(sketch, "E97.left", {"start": v(-4318, 3987.8) * mm, "end": v(-4318, 2794) * mm});
            skLineSegment(sketch, "E97.right", {"start": v(-3606.8, 3987.8) * mm, "end": v(-3606.8, 2794) * mm});
            skLineSegment(sketch, "E98.bottom", {"start": v(-4978.4, 2159) * mm, "end": v(-4267.2, 2159) * mm});
            skLineSegment(sketch, "E98.top", {"start": v(-4978.4, 711.2) * mm, "end": v(-4267.2, 711.2) * mm});
            skLineSegment(sketch, "E98.left", {"start": v(-4978.4, 2159) * mm, "end": v(-4978.4, 711.2) * mm});
            skLineSegment(sketch, "E98.right", {"start": v(-4267.2, 2159) * mm, "end": v(-4267.2, 711.2) * mm});
            skLineSegment(sketch, "E99.MirrorCS", {"start": v(-914.4, 2159) * mm, "end": v(-914.4, 711.2) * mm});
            skLineSegment(sketch, "E100.MirrorCS", {"start": v(-914.4, 2159) * mm, "end": v(-1625.6, 2159) * mm});
            skLineSegment(sketch, "E101.MirrorCS", {"start": v(-914.4, 711.2) * mm, "end": v(-1625.6, 711.2) * mm});
            skLineSegment(sketch, "E102.MirrorCS", {"start": v(-1574.8, 2794) * mm, "end": v(-2286, 2794) * mm});
            skLineSegment(sketch, "E103.MirrorCS", {"start": v(-1574.8, 3987.8) * mm, "end": v(-2286, 3987.8) * mm});
            skLineSegment(sketch, "E104.MirrorCS", {"start": v(-1625.6, 2159) * mm, "end": v(-1625.6, 711.2) * mm});
            skLineSegment(sketch, "E105.MirrorCS", {"start": v(-1574.8, 3987.8) * mm, "end": v(-1574.8, 2794) * mm});
            skLineSegment(sketch, "E106.MirrorCS", {"start": v(-2286, 3987.8) * mm, "end": v(-2286, 2794) * mm});
            skSolve(sketch);
        }
        {
            var Q0;
            Q0 = qSketchRegion(id + "F37", true);
            extrude(context, id + "F38", {"entities" : qUnion([Q0]), "operationType" : NewBodyOperationType.ADD, "depth" : 25.4 * mm});
        }
        {
            var Q0;
            Q0=makeQuery(id+"F38.opExtrude","CAP_FACE",FACE,{"disambiguationData":[OSD([sQuery(id+"F37.wireOp",EDGE,"E98.bottom"),sQuery(id+"F37.wireOp",EDGE,"E98.top"),sQuery(id+"F37.wireOp",EDGE,"E98.left"),sQuery(id+"F37.wireOp",EDGE,"E98.right")])],"isStart":false});
            var sketch = newSketch(context, id + "F39", { "sketchPlane" : qUnion([Q0])});
            skLineSegment(sketch, "E107.0", {"start": v(-3708.4, 3886.2) * mm, "end": v(-4216.4, 3886.2) * mm});
            skLineSegment(sketch, "E107.1", {"start": v(-3708.4, 2895.6) * mm, "end": v(-3708.4, 3886.2) * mm});
            skLineSegment(sketch, "E107.2", {"start": v(-4216.4, 2895.6) * mm, "end": v(-3708.4, 2895.6) * mm});
            skLineSegment(sketch, "E107.3", {"start": v(-4216.4, 3886.2) * mm, "end": v(-4216.4, 2895.6) * mm});
            skLineSegment(sketch, "E108.0", {"start": v(-2184.4, 2895.6) * mm, "end": v(-1676.4, 2895.6) * mm});
            skLineSegment(sketch, "E108.1", {"start": v(-2184.4, 3886.2) * mm, "end": v(-2184.4, 2895.6) * mm});
            skLineSegment(sketch, "E108.2", {"start": v(-1676.4, 3886.2) * mm, "end": v(-2184.4, 3886.2) * mm});
            skLineSegment(sketch, "E108.3", {"start": v(-1676.4, 2895.6) * mm, "end": v(-1676.4, 3886.2) * mm});
            skLineSegment(sketch, "E109.0", {"start": v(-4368.8, 2057.4) * mm, "end": v(-4876.8, 2057.4) * mm});
            skLineSegment(sketch, "E109.1", {"start": v(-4368.8, 812.8) * mm, "end": v(-4368.8, 2057.4) * mm});
            skLineSegment(sketch, "E109.2", {"start": v(-4876.8, 812.8) * mm, "end": v(-4368.8, 812.8) * mm});
            skLineSegment(sketch, "E109.3", {"start": v(-4876.8, 2057.4) * mm, "end": v(-4876.8, 812.8) * mm});
            skLineSegment(sketch, "E110.0", {"start": v(-1016, 812.8) * mm, "end": v(-1016, 2057.4) * mm});
            skLineSegment(sketch, "E110.1", {"start": v(-1524, 812.8) * mm, "end": v(-1016, 812.8) * mm});
            skLineSegment(sketch, "E110.2", {"start": v(-1524, 2057.4) * mm, "end": v(-1524, 812.8) * mm});
            skLineSegment(sketch, "E110.3", {"start": v(-1016, 2057.4) * mm, "end": v(-1524, 2057.4) * mm});
            skSolve(sketch);
        }
        {
            var Q0;
            Q0 = qSketchRegion(id + "F39", true);
            extrude(context, id + "F40", {"entities" : qUnion([Q0]), "operationType" : NewBodyOperationType.REMOVE, "oppositeDirection" : true, "depth" : 50.8 * mm});
        }
        {
            var Q0;
            Q0=makeQuery(id+"F18.boolean.opBoolean","MERGE",FACE,{"derivedFrom":[makeQuery(id+"F1.opExtrude","CAP_FACE",FACE,{"disambiguationData":[OSD([sQuery(id+"F0.wireOp",EDGE,"E0.bottom"),sQuery(id+"F0.wireOp",EDGE,"E0.top"),sQuery(id+"F0.wireOp",EDGE,"E0.left"),sQuery(id+"F0.wireOp",EDGE,"E0.right")])],"isStart":true}),makeQuery(id+"F18.opExtrude","CAP_FACE",FACE,{"disambiguationData":[OSD([sQuery(id+"F17.wireOp",EDGE,"E37.bottom"),sQuery(id+"F17.wireOp",EDGE,"E37.top"),sQuery(id+"F17.wireOp",EDGE,"E37.left"),sQuery(id+"F17.wireOp",EDGE,"E37.right")])],"isStart":true}),makeQuery(id+"F18.opExtrude","CAP_FACE",FACE,{"disambiguationData":[OSD([sQuery(id+"F17.wireOp",EDGE,"E38.bottom"),sQuery(id+"F17.wireOp",EDGE,"E38.top"),sQuery(id+"F17.wireOp",EDGE,"E38.left"),sQuery(id+"F17.wireOp",EDGE,"E38.right")])],"isStart":true}),makeQuery(id+"F18.opExtrude","CAP_FACE",FACE,{"disambiguationData":[OSD([sQuery(id+"F17.wireOp",EDGE,"E39.MirrorCS"),sQuery(id+"F17.wireOp",EDGE,"E44.MirrorCS"),sQuery(id+"F17.wireOp",EDGE,"E45.MirrorCS"),sQuery(id+"F17.wireOp",EDGE,"E46.MirrorCS")])],"isStart":true}),makeQuery(id+"F18.opExtrude","CAP_FACE",FACE,{"disambiguationData":[OSD([sQuery(id+"F17.wireOp",EDGE,"E40.MirrorCS"),sQuery(id+"F17.wireOp",EDGE,"E41.MirrorCS"),sQuery(id+"F17.wireOp",EDGE,"E42.MirrorCS"),sQuery(id+"F17.wireOp",EDGE,"E43.MirrorCS")])],"isStart":true})]});
            var sketch = newSketch(context, id + "F41", { "sketchPlane" : qUnion([Q0])});
            skLineSegment(sketch, "E111.0", {"start": v(76.2, -7289.8) * mm, "end": v(5816.6, -7289.8) * mm});
            skLineSegment(sketch, "E111.1", {"start": v(76.2, -76.2) * mm, "end": v(76.2, -7289.8) * mm});
            skLineSegment(sketch, "E111.2", {"start": v(76.2, -76.2) * mm, "end": v(5816.6, -76.2) * mm});
            skLineSegment(sketch, "E111.3", {"start": v(5816.6, -76.2) * mm, "end": v(5816.6, -7289.8) * mm});
            skSolve(sketch);
        }
        {
            var Q0;
            Q0 = qSketchRegion(id + "F41", true);
            extrude(context, id + "F42", {"entities" : qUnion([Q0]), "operationType" : NewBodyOperationType.ADD, "depth" : 2032 * mm});
        }
        {
            var Q0;
            {var subQ0=sQuery(id+"F0.wireOp",EDGE,"E0.bottom");Q0=makeQuery(id+"F3.boolean.opBoolean","MERGE",FACE,{"derivedFrom":[makeQuery(id+"F1.opExtrude","SWEPT_FACE",FACE,{"disambiguationData":[OSD([subQ0])]}),makeQuery(id+"F3.opExtrude","CAP_FACE",FACE,{"disambiguationData":[OSD([subQ0,sQuery(id+"F2.wireOp",EDGE,"E1"),sQuery(id+"F2.wireOp",EDGE,"E2")])],"isStart":true})]});}
            var sketch = newSketch(context, id + "F43", { "sketchPlane" : qUnion([Q0])});
            skLineSegment(sketch, "E112.bottom", {"start": v(736.6, 2394.1) * mm, "end": v(3810, 2394.1) * mm});
            skLineSegment(sketch, "E112.top", {"start": v(736.6, 2165.5) * mm, "end": v(3810, 2165.5) * mm});
            skLineSegment(sketch, "E112.left", {"start": v(736.6, 2394.1) * mm, "end": v(736.6, 2165.5) * mm});
            skLineSegment(sketch, "E112.right", {"start": v(3810, 2394.1) * mm, "end": v(3810, 2165.5) * mm});
            skSolve(sketch);
        }
        {
            var Q0;
            Q0 = qSketchRegion(id + "F43", true);
            extrude(context, id + "F44", {"entities" : qUnion([Q0]), "operationType" : NewBodyOperationType.ADD, "depth" : 1422.4 * mm});
        }
        {
            var Q0;
            Q0=makeQuery(id+"F44.opExtrude","SWEPT_FACE",FACE,{"disambiguationData":[OSD([sQuery(id+"F43.wireOp",EDGE,"E112.top")])]});
            var sketch = newSketch(context, id + "F45", { "sketchPlane" : qUnion([Q0])});
            skLineSegment(sketch, "E113.0", {"start": v(774.7, 38.1) * mm, "end": v(3771.9, 38.1) * mm});
            skLineSegment(sketch, "E113.1", {"start": v(774.7, 1384.3) * mm, "end": v(774.7, 38.1) * mm});
            skLineSegment(sketch, "E113.2", {"start": v(3771.9, 1384.3) * mm, "end": v(774.7, 1384.3) * mm});
            skLineSegment(sketch, "E113.3", {"start": v(3771.9, 38.1) * mm, "end": v(3771.9, 1384.3) * mm});
            skSolve(sketch);
        }
        {
            var Q0;
            Q0 = qSketchRegion(id + "F45", true);
            extrude(context, id + "F46", {"entities" : qUnion([Q0]), "operationType" : NewBodyOperationType.REMOVE, "oppositeDirection" : true, "depth" : 177.8 * mm});
        }
        {
            var Q0;
            Q0=makeQuery(id+"F24.opExtrude","CAP_FACE",FACE,{"disambiguationData":[OSD([sQuery(id+"F23.wireOp",EDGE,"E55.MirrorCS"),sQuery(id+"F23.wireOp",EDGE,"E56.MirrorCS"),sQuery(id+"F23.wireOp",EDGE,"E58.MirrorCS"),sQuery(id+"F23.wireOp",EDGE,"E62.MirrorCS")])],"isStart":false});
            var sketch = newSketch(context, id + "F47", { "sketchPlane" : qUnion([Q0])});
            skLineSegment(sketch, "E114", {"start": v(3810, 2165.5) * mm, "end": v(6587.07, -120.5) * mm});
            skLineSegment(sketch, "E115", {"start": v(6587.07, -120.5) * mm, "end": v(6818.49, -120.5) * mm});
            skLineSegment(sketch, "E116", {"start": v(6124.22, 451) * mm, "end": v(6124.22, 641.5) * mm});
            skLineSegment(sketch, "E117", {"start": v(6124.22, 641.5) * mm, "end": v(5892.8, 641.5) * mm});
            skLineSegment(sketch, "E118", {"start": v(5892.8, 641.5) * mm, "end": v(5892.8, 832) * mm});
            skLineSegment(sketch, "E119", {"start": v(5892.8, 832) * mm, "end": v(5661.38, 832) * mm});
            skLineSegment(sketch, "E120", {"start": v(5661.38, 832) * mm, "end": v(5661.38, 1022.5) * mm});
            skLineSegment(sketch, "E121", {"start": v(5661.38, 1022.5) * mm, "end": v(5429.96, 1022.5) * mm});
            skLineSegment(sketch, "E122", {"start": v(5429.96, 1022.5) * mm, "end": v(5429.96, 1213) * mm});
            skLineSegment(sketch, "E123", {"start": v(5429.96, 1213) * mm, "end": v(5198.53, 1213) * mm});
            skLineSegment(sketch, "E124", {"start": v(5198.53, 1213) * mm, "end": v(5198.53, 1403.5) * mm});
            skLineSegment(sketch, "E125", {"start": v(5198.53, 1403.5) * mm, "end": v(4967.11, 1403.5) * mm});
            skLineSegment(sketch, "E126", {"start": v(4967.11, 1403.5) * mm, "end": v(4967.11, 1594) * mm});
            skLineSegment(sketch, "E127", {"start": v(4967.11, 1594) * mm, "end": v(4735.69, 1594) * mm});
            skLineSegment(sketch, "E128", {"start": v(4735.69, 1594) * mm, "end": v(4735.69, 1784.5) * mm});
            skLineSegment(sketch, "E129", {"start": v(4735.69, 1784.5) * mm, "end": v(4504.27, 1784.5) * mm});
            skLineSegment(sketch, "E130", {"start": v(4504.27, 1784.5) * mm, "end": v(4504.27, 1975) * mm});
            skLineSegment(sketch, "E131", {"start": v(4504.27, 1975) * mm, "end": v(4272.84, 1975) * mm});
            skLineSegment(sketch, "E132", {"start": v(4272.84, 1975) * mm, "end": v(4272.84, 2165.5) * mm});
            skLineSegment(sketch, "E133", {"start": v(4272.84, 2165.5) * mm, "end": v(4041.42, 2165.5) * mm});
            skLineSegment(sketch, "E134", {"start": v(4041.42, 2165.5) * mm, "end": v(4041.42, 2356) * mm});
            skLineSegment(sketch, "E135", {"start": v(4041.42, 2356) * mm, "end": v(3810, 2356) * mm});
            skLineSegment(sketch, "E136", {"start": v(3810, 2356) * mm, "end": v(3810, 2165.5) * mm});
            skLineSegment(sketch, "E137", {"start": v(6124.22, 451) * mm, "end": v(6355.64, 451) * mm});
            skLineSegment(sketch, "E138", {"start": v(6355.64, 451) * mm, "end": v(6355.64, 260.5) * mm});
            skLineSegment(sketch, "E139", {"start": v(6355.64, 260.5) * mm, "end": v(6587.07, 260.5) * mm});
            skLineSegment(sketch, "E140", {"start": v(6587.07, 260.5) * mm, "end": v(6587.07, 70) * mm});
            skLineSegment(sketch, "E141", {"start": v(6587.07, 70) * mm, "end": v(6818.49, 70) * mm});
            skLineSegment(sketch, "E142", {"start": v(6818.49, 70) * mm, "end": v(6818.49, -120.5) * mm});
            skSolve(sketch);
        }
        {
            var Q0;
            Q0 = qSketchRegion(id + "F47", true);
            extrude(context, id + "F48", {"entities" : qUnion([Q0]), "operationType" : NewBodyOperationType.ADD, "depth" : 1066.8 * mm});
        }
        {
            var Q0;
            Q0=makeQuery(id+"F48.opExtrude","SWEPT_FACE",FACE,{"disambiguationData":[OSD([sQuery(id+"F47.wireOp",EDGE,"E135")])]});
            var sketch = newSketch(context, id + "F49", { "sketchPlane" : qUnion([Q0])});
            skLineSegment(sketch, "E143.bottom", {"start": v(3810, -539.75) * mm, "end": v(6819.54, -539.75) * mm});
            skLineSegment(sketch, "E143.top", {"start": v(3810, -63.5) * mm, "end": v(6819.54, -63.5) * mm});
            skLineSegment(sketch, "E143.left", {"start": v(3810, -539.75) * mm, "end": v(3810, -63.5) * mm});
            skLineSegment(sketch, "E143.right", {"start": v(6819.54, -539.75) * mm, "end": v(6819.54, -63.5) * mm});
            skLineSegment(sketch, "E144.bottom", {"start": v(3810, -577.85) * mm, "end": v(6819.54, -577.85) * mm});
            skLineSegment(sketch, "E144.top", {"start": v(3810, -1054.1) * mm, "end": v(6819.54, -1054.1) * mm});
            skLineSegment(sketch, "E144.left", {"start": v(3810, -577.85) * mm, "end": v(3810, -1054.1) * mm});
            skLineSegment(sketch, "E144.right", {"start": v(6819.54, -577.85) * mm, "end": v(6819.54, -1054.1) * mm});
            skSolve(sketch);
        }
        {
            var Q0;
            Q0 = qSketchRegion(id + "F49", true);
            var Q1;
            Q1=makeQuery(id+"F48.opExtrude","SWEPT_FACE",FACE,{"disambiguationData":[OSD([sQuery(id+"F47.wireOp",EDGE,"E115")])]});
            extrude(context, id + "F50", {"entities" : qUnion([Q0]), "operationType" : NewBodyOperationType.REMOVE, "endBound" : BoundingType.UP_TO_SURFACE, "oppositeDirection" : true, "endBoundEntityFace" : qUnion([Q1]), "depth" : 25.4 * mm});
        }
        {
            var Q0;
            {var subQ5=sQuery(id+"F23.wireOp",EDGE,"E56.MirrorCS");var subQ6=sQuery(id+"F23.wireOp",EDGE,"E62.MirrorCS");Q0=makeQuery(id+"F48.boolean.opBoolean","SPLIT",FACE,{"disambiguationData":[TD([makeQuery(id+"F24.opExtrude","SWEPT_FACE",FACE,{"disambiguationData":[OSD([subQ6])]})])],"derivedFrom":makeQuery(id+"F24.opExtrude","CAP_FACE",FACE,{"disambiguationData":[OSD([sQuery(id+"F23.wireOp",EDGE,"E55.MirrorCS"),subQ5,sQuery(id+"F23.wireOp",EDGE,"E58.MirrorCS"),subQ6])],"isStart":false})});}
            var sketch = newSketch(context, id + "F51", { "sketchPlane" : qUnion([Q0])});
            skLineSegment(sketch, "E145.bottom", {"start": v(3810, 2356) * mm, "end": v(4064, 2356) * mm});
            skLineSegment(sketch, "E145.top", {"start": v(3810, 2387.75) * mm, "end": v(4064, 2387.75) * mm});
            skLineSegment(sketch, "E145.left", {"start": v(3810, 2356) * mm, "end": v(3810, 2387.75) * mm});
            skLineSegment(sketch, "E145.right", {"start": v(4064, 2356) * mm, "end": v(4064, 2387.75) * mm});
            skLineSegment(sketch, "E146.bottom", {"start": v(4041.42, 2165.5) * mm, "end": v(4295.42, 2165.5) * mm});
            skLineSegment(sketch, "E146.top", {"start": v(4041.42, 2197.25) * mm, "end": v(4295.42, 2197.25) * mm});
            skLineSegment(sketch, "E146.left", {"start": v(4041.42, 2165.5) * mm, "end": v(4041.42, 2197.25) * mm});
            skLineSegment(sketch, "E146.right", {"start": v(4295.42, 2165.5) * mm, "end": v(4295.42, 2197.25) * mm});
            skLineSegment(sketch, "E147.bottom", {"start": v(4504.27, 1784.5) * mm, "end": v(4758.27, 1784.5) * mm});
            skLineSegment(sketch, "E147.top", {"start": v(4504.27, 1816.25) * mm, "end": v(4758.27, 1816.25) * mm});
            skLineSegment(sketch, "E147.left", {"start": v(4504.27, 1784.5) * mm, "end": v(4504.27, 1816.25) * mm});
            skLineSegment(sketch, "E147.right", {"start": v(4758.27, 1784.5) * mm, "end": v(4758.27, 1816.25) * mm});
            skLineSegment(sketch, "E148.bottom", {"start": v(4735.69, 1594) * mm, "end": v(4989.69, 1594) * mm});
            skLineSegment(sketch, "E148.top", {"start": v(4735.69, 1625.75) * mm, "end": v(4989.69, 1625.75) * mm});
            skLineSegment(sketch, "E148.left", {"start": v(4735.69, 1594) * mm, "end": v(4735.69, 1625.75) * mm});
            skLineSegment(sketch, "E148.right", {"start": v(4989.69, 1594) * mm, "end": v(4989.69, 1625.75) * mm});
            skLineSegment(sketch, "E149.bottom", {"start": v(4967.11, 1403.5) * mm, "end": v(5221.11, 1403.5) * mm});
            skLineSegment(sketch, "E149.top", {"start": v(4967.11, 1435.25) * mm, "end": v(5221.11, 1435.25) * mm});
            skLineSegment(sketch, "E149.left", {"start": v(4967.11, 1403.5) * mm, "end": v(4967.11, 1435.25) * mm});
            skLineSegment(sketch, "E149.right", {"start": v(5221.11, 1403.5) * mm, "end": v(5221.11, 1435.25) * mm});
            skLineSegment(sketch, "E150.bottom", {"start": v(5198.53, 1213) * mm, "end": v(5452.53, 1213) * mm});
            skLineSegment(sketch, "E150.top", {"start": v(5198.53, 1244.75) * mm, "end": v(5452.53, 1244.75) * mm});
            skLineSegment(sketch, "E150.left", {"start": v(5198.53, 1213) * mm, "end": v(5198.53, 1244.75) * mm});
            skLineSegment(sketch, "E150.right", {"start": v(5452.53, 1213) * mm, "end": v(5452.53, 1244.75) * mm});
            skLineSegment(sketch, "E151.bottom", {"start": v(5429.96, 1022.5) * mm, "end": v(5683.96, 1022.5) * mm});
            skLineSegment(sketch, "E151.top", {"start": v(5429.96, 1054.25) * mm, "end": v(5683.96, 1054.25) * mm});
            skLineSegment(sketch, "E151.left", {"start": v(5429.96, 1022.5) * mm, "end": v(5429.96, 1054.25) * mm});
            skLineSegment(sketch, "E151.right", {"start": v(5683.96, 1022.5) * mm, "end": v(5683.96, 1054.25) * mm});
            skLineSegment(sketch, "E152.bottom", {"start": v(5661.38, 832) * mm, "end": v(5915.38, 832) * mm});
            skLineSegment(sketch, "E152.top", {"start": v(5661.38, 863.75) * mm, "end": v(5915.38, 863.75) * mm});
            skLineSegment(sketch, "E152.left", {"start": v(5661.38, 832) * mm, "end": v(5661.38, 863.75) * mm});
            skLineSegment(sketch, "E152.right", {"start": v(5915.38, 832) * mm, "end": v(5915.38, 863.75) * mm});
            skLineSegment(sketch, "E153.bottom", {"start": v(5892.8, 641.5) * mm, "end": v(6146.8, 641.5) * mm});
            skLineSegment(sketch, "E153.top", {"start": v(5892.8, 673.25) * mm, "end": v(6146.8, 673.25) * mm});
            skLineSegment(sketch, "E153.left", {"start": v(5892.8, 641.5) * mm, "end": v(5892.8, 673.25) * mm});
            skLineSegment(sketch, "E153.right", {"start": v(6146.8, 641.5) * mm, "end": v(6146.8, 673.25) * mm});
            skLineSegment(sketch, "E154.bottom", {"start": v(6124.22, 451) * mm, "end": v(6378.22, 451) * mm});
            skLineSegment(sketch, "E154.top", {"start": v(6124.22, 482.75) * mm, "end": v(6378.22, 482.75) * mm});
            skLineSegment(sketch, "E154.left", {"start": v(6124.22, 451) * mm, "end": v(6124.22, 482.75) * mm});
            skLineSegment(sketch, "E154.right", {"start": v(6378.22, 451) * mm, "end": v(6378.22, 482.75) * mm});
            skLineSegment(sketch, "E155.bottom", {"start": v(6355.64, 260.5) * mm, "end": v(6609.64, 260.5) * mm});
            skLineSegment(sketch, "E155.top", {"start": v(6355.64, 292.25) * mm, "end": v(6609.64, 292.25) * mm});
            skLineSegment(sketch, "E155.left", {"start": v(6355.64, 260.5) * mm, "end": v(6355.64, 292.25) * mm});
            skLineSegment(sketch, "E155.right", {"start": v(6609.64, 260.5) * mm, "end": v(6609.64, 292.25) * mm});
            skLineSegment(sketch, "E156.bottom", {"start": v(6587.07, 70) * mm, "end": v(6841.07, 70) * mm});
            skLineSegment(sketch, "E156.top", {"start": v(6587.07, 101.75) * mm, "end": v(6841.07, 101.75) * mm});
            skLineSegment(sketch, "E156.left", {"start": v(6587.07, 70) * mm, "end": v(6587.07, 101.75) * mm});
            skLineSegment(sketch, "E156.right", {"start": v(6841.07, 70) * mm, "end": v(6841.07, 101.75) * mm});
            skLineSegment(sketch, "E157.bottom", {"start": v(4272.84, 1975) * mm, "end": v(4526.84, 1975) * mm});
            skLineSegment(sketch, "E157.top", {"start": v(4272.84, 2006.75) * mm, "end": v(4526.84, 2006.75) * mm});
            skLineSegment(sketch, "E157.left", {"start": v(4272.84, 1975) * mm, "end": v(4272.84, 2006.75) * mm});
            skLineSegment(sketch, "E157.right", {"start": v(4526.84, 1975) * mm, "end": v(4526.84, 2006.75) * mm});
            skSolve(sketch);
        }
        {
            var Q0;
            Q0 = qSketchRegion(id + "F51", true);
            extrude(context, id + "F52", {"entities" : qUnion([Q0]), "operationType" : NewBodyOperationType.ADD, "depth" : 1102.36 * mm});
        }
        {
            var Q0;
            Q0=makeQuery(id+"F44.opExtrude","SWEPT_FACE",FACE,{"disambiguationData":[OSD([sQuery(id+"F43.wireOp",EDGE,"E112.bottom")])]});
            var sketch = newSketch(context, id + "F53", { "sketchPlane" : qUnion([Q0])});
            skLineSegment(sketch, "E158.bottom", {"start": v(787.4, -1282.7) * mm, "end": v(876.3, -1282.7) * mm});
            skLineSegment(sketch, "E158.top", {"start": v(787.4, -1371.6) * mm, "end": v(876.3, -1371.6) * mm});
            skLineSegment(sketch, "E158.left", {"start": v(787.4, -1282.7) * mm, "end": v(787.4, -1371.6) * mm});
            skLineSegment(sketch, "E158.right", {"start": v(876.3, -1282.7) * mm, "end": v(876.3, -1371.6) * mm});
            skLineSegment(sketch, "E159.bottom", {"start": v(2206.12, -1282.7) * mm, "end": v(2295.02, -1282.7) * mm});
            skLineSegment(sketch, "E159.top", {"start": v(2206.12, -1371.6) * mm, "end": v(2295.02, -1371.6) * mm});
            skLineSegment(sketch, "E159.left", {"start": v(2206.12, -1282.7) * mm, "end": v(2206.12, -1371.6) * mm});
            skLineSegment(sketch, "E159.right", {"start": v(2295.02, -1282.7) * mm, "end": v(2295.02, -1371.6) * mm});
            skLineSegment(sketch, "E160.bottom", {"start": v(3670.3, -1282.7) * mm, "end": v(3759.2, -1282.7) * mm});
            skLineSegment(sketch, "E160.top", {"start": v(3670.3, -1371.6) * mm, "end": v(3759.2, -1371.6) * mm});
            skLineSegment(sketch, "E160.left", {"start": v(3670.3, -1282.7) * mm, "end": v(3670.3, -1371.6) * mm});
            skLineSegment(sketch, "E160.right", {"start": v(3759.2, -1282.7) * mm, "end": v(3759.2, -1371.6) * mm});
            skLineSegment(sketch, "E161.bottom", {"start": v(3670.3, -1092.2) * mm, "end": v(3759.2, -1092.2) * mm});
            skLineSegment(sketch, "E161.top", {"start": v(3670.3, -1181.1) * mm, "end": v(3759.2, -1181.1) * mm});
            skLineSegment(sketch, "E161.left", {"start": v(3670.3, -1092.2) * mm, "end": v(3670.3, -1181.1) * mm});
            skLineSegment(sketch, "E161.right", {"start": v(3759.2, -1092.2) * mm, "end": v(3759.2, -1181.1) * mm});
            skLineSegment(sketch, "E162.bottom", {"start": v(787.4, -12.7) * mm, "end": v(876.3, -12.7) * mm});
            skLineSegment(sketch, "E162.top", {"start": v(787.4, -101.6) * mm, "end": v(876.3, -101.6) * mm});
            skLineSegment(sketch, "E162.left", {"start": v(787.4, -12.7) * mm, "end": v(787.4, -101.6) * mm});
            skLineSegment(sketch, "E162.right", {"start": v(876.3, -12.7) * mm, "end": v(876.3, -101.6) * mm});
            skSolve(sketch);
        }
        {
            var Q0;
            Q0 = qSketchRegion(id + "F53", true);
            extrude(context, id + "F54", {"entities" : qUnion([Q0]), "operationType" : NewBodyOperationType.ADD, "depth" : 965.2 * mm, "hasSecondDirection" : true, "secondDirectionOppositeDirection" : true, "secondDirectionDepth" : 3048 * mm});
        }
        {
            var Q0;
            Q0=makeQuery(id+"F54.opExtrude","CAP_FACE",FACE,{"disambiguationData":[OSD([sQuery(id+"F53.wireOp",EDGE,"E159.bottom"),sQuery(id+"F53.wireOp",EDGE,"E159.top"),sQuery(id+"F53.wireOp",EDGE,"E159.left"),sQuery(id+"F53.wireOp",EDGE,"E159.right")])],"isStart":true});
            var sketch = newSketch(context, id + "F55", { "sketchPlane" : qUnion([Q0])});
            skLineSegment(sketch, "E163.0.0", {"start": v(2206.12, 1282.7) * mm, "end": v(2295.02, 1282.7) * mm});
            skLineSegment(sketch, "E163.0.1", {"start": v(2295.02, 1282.7) * mm, "end": v(2295.02, 1371.6) * mm});
            skLineSegment(sketch, "E163.0.2", {"start": v(2295.02, 1371.6) * mm, "end": v(2206.12, 1371.6) * mm});
            skLineSegment(sketch, "E163.0.3", {"start": v(2206.12, 1371.6) * mm, "end": v(2206.12, 1282.7) * mm});
            skLineSegment(sketch, "E164.0.0", {"start": v(3670.3, 1092.2) * mm, "end": v(3759.2, 1092.2) * mm});
            skLineSegment(sketch, "E164.0.1", {"start": v(3759.2, 1092.2) * mm, "end": v(3759.2, 1181.1) * mm});
            skLineSegment(sketch, "E164.0.2", {"start": v(3759.2, 1181.1) * mm, "end": v(3670.3, 1181.1) * mm});
            skLineSegment(sketch, "E164.0.3", {"start": v(3670.3, 1181.1) * mm, "end": v(3670.3, 1092.2) * mm});
            skSolve(sketch);
        }
        {
            var Q0;
            Q0 = qSketchRegion(id + "F55", true);
            var Q1;
            Q1=makeQuery(id+"F44.opExtrude","SWEPT_FACE",FACE,{"disambiguationData":[OSD([sQuery(id+"F43.wireOp",EDGE,"E112.top")])]});
            extrude(context, id + "F56", {"entities" : qUnion([Q0]), "operationType" : NewBodyOperationType.REMOVE, "endBound" : BoundingType.UP_TO_SURFACE, "oppositeDirection" : true, "endBoundEntityFace" : qUnion([Q1]), "depth" : 25.4 * mm});
        }
        {
            var Q0;
            Q0=makeQuery(id+"F48.opExtrude","CAP_FACE",FACE,{"disambiguationData":[OSD([sQuery(id+"F47.wireOp",EDGE,"E114"),sQuery(id+"F47.wireOp",EDGE,"E115"),sQuery(id+"F47.wireOp",EDGE,"E116"),sQuery(id+"F47.wireOp",EDGE,"E117"),sQuery(id+"F47.wireOp",EDGE,"E118"),sQuery(id+"F47.wireOp",EDGE,"E119"),sQuery(id+"F47.wireOp",EDGE,"E120"),sQuery(id+"F47.wireOp",EDGE,"E121"),sQuery(id+"F47.wireOp",EDGE,"E122"),sQuery(id+"F47.wireOp",EDGE,"E123"),sQuery(id+"F47.wireOp",EDGE,"E124"),sQuery(id+"F47.wireOp",EDGE,"E125"),sQuery(id+"F47.wireOp",EDGE,"E126"),sQuery(id+"F47.wireOp",EDGE,"E127"),sQuery(id+"F47.wireOp",EDGE,"E128"),sQuery(id+"F47.wireOp",EDGE,"E129"),sQuery(id+"F47.wireOp",EDGE,"E130"),sQuery(id+"F47.wireOp",EDGE,"E131"),sQuery(id+"F47.wireOp",EDGE,"E132"),sQuery(id+"F47.wireOp",EDGE,"E133"),sQuery(id+"F47.wireOp",EDGE,"E134"),sQuery(id+"F47.wireOp",EDGE,"E135"),sQuery(id+"F47.wireOp",EDGE,"E136"),sQuery(id+"F47.wireOp",EDGE,"E137"),sQuery(id+"F47.wireOp",EDGE,"E138"),sQuery(id+"F47.wireOp",EDGE,"E139"),sQuery(id+"F47.wireOp",EDGE,"E140"),sQuery(id+"F47.wireOp",EDGE,"E141"),sQuery(id+"F47.wireOp",EDGE,"E142")])],"isStart":false});
            var sketch = newSketch(context, id + "F57", { "sketchPlane" : qUnion([Q0])});
            skPoint(sketch, "E165.oppositeSnap0", {"position": v(5661.38, 943.12) * mm});
            skLineSegment(sketch, "E165.bottom", {"start": v(5572.48, 714.68) * mm, "end": v(5661.38, 714.68) * mm});
            skLineSegment(sketch, "E165.top", {"start": v(5572.48, 1765.45) * mm, "end": v(5661.38, 1765.45) * mm});
            skLineSegment(sketch, "E165.left", {"start": v(5572.48, 714.68) * mm, "end": v(5572.48, 1765.45) * mm});
            skLineSegment(sketch, "E165.right", {"start": v(5661.38, 714.68) * mm, "end": v(5661.38, 1765.45) * mm});
            skLineSegment(sketch, "E166.bottom", {"start": v(6498.17, 0) * mm, "end": v(6587.07, 0) * mm});
            skLineSegment(sketch, "E166.left", {"start": v(6498.17, 0) * mm, "end": v(6498.17, 1003.45) * mm});
            skLineSegment(sketch, "E166.right", {"start": v(6587.07, 0) * mm, "end": v(6587.07, 1003.45) * mm});
            skLineSegment(sketch, "E167", {"start": v(6498.17, 1003.45) * mm, "end": v(6587.07, 1003.45) * mm});
            skSolve(sketch);
        }
        {
            var Q0;
            Q0 = qSketchRegion(id + "F57", true);
            extrude(context, id + "F58", {"entities" : qUnion([Q0]), "operationType" : NewBodyOperationType.ADD, "depth" : 88.9 * mm});
        }
        {
            var Q0;
            Q0=makeQuery(id+"F54.opExtrude","CAP_FACE",FACE,{"disambiguationData":[OSD([sQuery(id+"F53.wireOp",EDGE,"E158.bottom"),sQuery(id+"F53.wireOp",EDGE,"E158.top"),sQuery(id+"F53.wireOp",EDGE,"E158.left"),sQuery(id+"F53.wireOp",EDGE,"E158.right")])],"isStart":false});
            var sketch = newSketch(context, id + "F59", { "sketchPlane" : qUnion([Q0])});
            skLineSegment(sketch, "E168", {"start": v(762, -1397) * mm, "end": v(3784.6, -1397) * mm});
            skLineSegment(sketch, "E169", {"start": v(3784.6, -1397) * mm, "end": v(3784.6, -1066.8) * mm});
            skLineSegment(sketch, "E170", {"start": v(3784.6, -1066.8) * mm, "end": v(3644.9, -1066.8) * mm});
            skLineSegment(sketch, "E171", {"start": v(3644.9, -1066.8) * mm, "end": v(3644.9, -1257.3) * mm});
            skLineSegment(sketch, "E172", {"start": v(3644.9, -1257.3) * mm, "end": v(901.7, -1257.3) * mm});
            skLineSegment(sketch, "E173", {"start": v(901.7, -1257.3) * mm, "end": v(901.7, -12.7) * mm});
            skLineSegment(sketch, "E174", {"start": v(901.7, -12.7) * mm, "end": v(762, -12.7) * mm});
            skLineSegment(sketch, "E175", {"start": v(762, -12.7) * mm, "end": v(762, -1397) * mm});
            skSolve(sketch);
        }
        {
            var Q0;
            Q0 = qSketchRegion(id + "F59", true);
            extrude(context, id + "F60", {"entities" : qUnion([Q0]), "operationType" : NewBodyOperationType.ADD, "depth" : 25.4 * mm});
        }
        {
            var Q0;
            Q0=makeQuery(id+"F58.opExtrude","CAP_FACE",FACE,{"disambiguationData":[OSD([sQuery(id+"F57.wireOp",EDGE,"E165.bottom"),sQuery(id+"F57.wireOp",EDGE,"E165.top"),sQuery(id+"F57.wireOp",EDGE,"E165.left"),sQuery(id+"F57.wireOp",EDGE,"E165.right")])],"isStart":false});
            var sketch = newSketch(context, id + "F61", { "sketchPlane" : qUnion([Q0])});
            skLineSegment(sketch, "E176", {"start": v(3759.2, 3333.9) * mm, "end": v(6746, 875.26) * mm});
            skLineSegment(sketch, "E177", {"start": v(6746, 875.26) * mm, "end": v(6725.81, 850.75) * mm});
            skLineSegment(sketch, "E178", {"start": v(6725.81, 850.75) * mm, "end": v(3759.2, 3292.78) * mm});
            skLineSegment(sketch, "E179", {"start": v(3759.2, 3292.78) * mm, "end": v(3759.2, 3333.9) * mm});
            skSolve(sketch);
        }
        {
            var Q0;
            Q0 = qSketchRegion(id + "F61", true);
            extrude(context, id + "F62", {"entities" : qUnion([Q0]), "operationType" : NewBodyOperationType.ADD, "depth" : 25.4 * mm, "hasSecondDirection" : true, "secondDirectionOppositeDirection" : true, "secondDirectionDepth" : 114.3 * mm});
        }
        {
            var Q0;
            {var subQ0=sQuery(id+"F53.wireOp",EDGE,"E158.left");var subQ1=sQuery(id+"F53.wireOp",EDGE,"E158.top");Q0=makeQuery(id+"F54.boolean.opBoolean","SPLIT",EDGE,{"disambiguationData":[TD([makeQuery(id+"F44.opExtrude","SWEPT_FACE",FACE,{"disambiguationData":[OSD([sQuery(id+"F43.wireOp",EDGE,"E112.bottom")])]})])],"derivedFrom":makeQuery(id+"F54.opExtrude","SWEPT_EDGE",EDGE,{"disambiguationData":[OSD([subQ1,subQ0])]})});}
            cPoint(context, id + "F63", {"entities" : qUnion([Q0]), "parameter" : 0.5});
        }
        {
            var Q0;
            Q0=makeQuery(id+"F44.opExtrude","SWEPT_FACE",FACE,{"disambiguationData":[OSD([sQuery(id+"F43.wireOp",EDGE,"E112.bottom")])]});
            var Q1;
            Q1 = qCreatedBy(id + "F63" ,VERTEX);
            cPlane(context, id + "F64", {"entities" : qUnion([Q0, Q1]), "cplaneType" : CPlaneType.PLANE_POINT, "offset" : 25.4 * mm, "width" : 152.4 * mm, "height" : 152.4 * mm});
        }
        {
            var Q0;
            Q0=qCreatedBy(id+"F64.planeOp",FACE);
            var sketch = newSketch(context, id + "F65", { "sketchPlane" : qUnion([Q0])});
            skLineSegment(sketch, "E180", {"start": v(749.3, 0) * mm, "end": v(749.3, -1409.7) * mm});
            skLineSegment(sketch, "E181", {"start": v(749.3, -1409.7) * mm, "end": v(3797.3, -1409.7) * mm});
            skLineSegment(sketch, "E182", {"start": v(3797.3, -1409.7) * mm, "end": v(3797.3, -1092.2) * mm});
            skLineSegment(sketch, "E183", {"start": v(3797.3, -1092.2) * mm, "end": v(3759.2, -1092.2) * mm});
            skLineSegment(sketch, "E184", {"start": v(3759.2, -1092.2) * mm, "end": v(3759.2, -1371.6) * mm});
            skLineSegment(sketch, "E185", {"start": v(3759.2, -1371.6) * mm, "end": v(787.4, -1371.6) * mm});
            skLineSegment(sketch, "E186", {"start": v(787.4, -1371.6) * mm, "end": v(787.4, 0) * mm});
            skLineSegment(sketch, "E187", {"start": v(787.4, 0) * mm, "end": v(749.3, 0) * mm});
            skSolve(sketch);
        }
        {
            var Q0;
            Q0 = qSketchRegion(id + "F65", true);
            extrude(context, id + "F66", {"entities" : qUnion([Q0]), "operationType" : NewBodyOperationType.ADD, "depth" : 88.9 * mm});
        }
        {
            var Q0;
            Q0=makeQuery(id+"F58.opExtrude","CAP_FACE",FACE,{"disambiguationData":[OSD([sQuery(id+"F57.wireOp",EDGE,"E165.bottom"),sQuery(id+"F57.wireOp",EDGE,"E165.top"),sQuery(id+"F57.wireOp",EDGE,"E165.left"),sQuery(id+"F57.wireOp",EDGE,"E165.right")])],"isStart":false});
            var sketch = newSketch(context, id + "F67", { "sketchPlane" : qUnion([Q0])});
            skLineSegment(sketch, "E188", {"start": v(3797.3, 2965.6) * mm, "end": v(6587.07, 669.14) * mm});
            skLineSegment(sketch, "E189", {"start": v(6587.07, 669.14) * mm, "end": v(6587.07, 554) * mm});
            skLineSegment(sketch, "E190", {"start": v(6587.07, 554) * mm, "end": v(3797.3, 2850.45) * mm});
            skLineSegment(sketch, "E191", {"start": v(3797.3, 2850.45) * mm, "end": v(3797.3, 2965.6) * mm});
            skSolve(sketch);
        }
        {
            var Q0;
            Q0 = qSketchRegion(id + "F67", true);
            extrude(context, id + "F68", {"entities" : qUnion([Q0]), "operationType" : NewBodyOperationType.ADD, "depth" : 38.1 * mm});
        }
        {
            var Q0;
            Q0=makeQuery(id+"F42.opExtrude","CAP_FACE",FACE,{"disambiguationData":[OSD([sQuery(id+"F41.wireOp",EDGE,"E111.0"),sQuery(id+"F41.wireOp",EDGE,"E111.1"),sQuery(id+"F41.wireOp",EDGE,"E111.2"),sQuery(id+"F41.wireOp",EDGE,"E111.3")])],"isStart":false});
            var sketch = newSketch(context, id + "F69", { "sketchPlane" : qUnion([Q0])});
            skLineSegment(sketch, "E192.bottom", {"start": v(416.08, -1635.6) * mm, "end": v(493.2, -1635.6) * mm});
            skLineSegment(sketch, "E192.top", {"start": v(416.08, -1558.47) * mm, "end": v(493.2, -1558.47) * mm});
            skLineSegment(sketch, "E192.left", {"start": v(416.08, -1635.6) * mm, "end": v(416.08, -1558.47) * mm});
            skLineSegment(sketch, "E192.right", {"start": v(493.2, -1635.6) * mm, "end": v(493.2, -1558.47) * mm});
            skSolve(sketch);
        }
        {
            var Q0;
            Q0 = qSketchRegion(id + "F69", true);
            extrude(context, id + "F70", {"entities" : qUnion([Q0]), "operationType" : NewBodyOperationType.ADD, "oppositeDirection" : true, "depth" : 6273.8 * mm});
        }
    });
